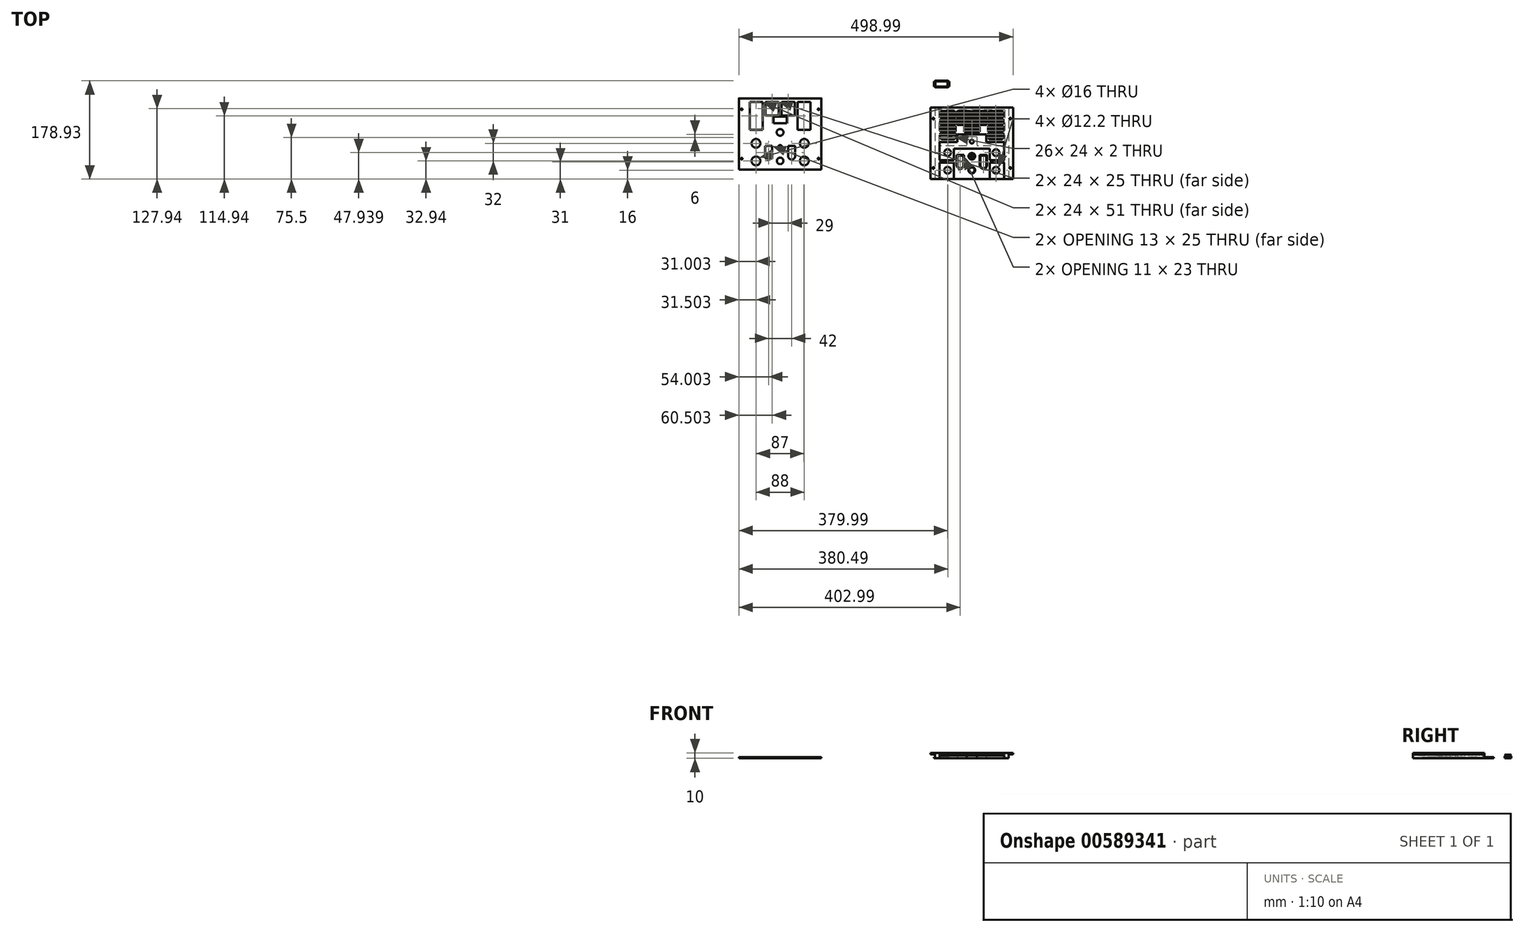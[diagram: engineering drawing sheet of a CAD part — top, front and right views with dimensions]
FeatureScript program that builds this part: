
annotation { "Feature Type Name" : "Feature", "Feature Type Description" : "" }
export const myFeature = defineFeature(function(context is Context, id is Id, definition is map)
    precondition{}
    {
        {
            var Q0;
            Q0=qCreatedBy(makeId("Top.planeOp"),FACE);
            var sketch = newSketch(context, id + "F0", { "sketchPlane" : qUnion([Q0])});
            skLineSegment(sketch, "E0.bottom", {"start": v(75, -65) * mm, "end": v(-75, -65) * mm});
            skLineSegment(sketch, "E0.top", {"start": v(75, 65) * mm, "end": v(-75, 65) * mm});
            skLineSegment(sketch, "E0.left", {"start": v(75, -65) * mm, "end": v(75, 65) * mm});
            skLineSegment(sketch, "E0.right", {"start": v(-75, -65) * mm, "end": v(-75, 65) * mm});
            skPoint(sketch, "E0.middle", {"position": v(0, 0) * mm});
            skLineSegment(sketch, "E1.bottom", {"start": v(-75, 65) * mm, "end": v(-65, 65) * mm, "construction": true});
            skLineSegment(sketch, "E1.top", {"start": v(-75, -65) * mm, "end": v(-65, -65) * mm, "construction": true});
            skLineSegment(sketch, "E1.left", {"start": v(-75, 65) * mm, "end": v(-75, -65) * mm, "construction": true});
            skLineSegment(sketch, "E1.right", {"start": v(-65, 65) * mm, "end": v(-65, -65) * mm, "construction": true});
            skLineSegment(sketch, "E2.bottom", {"start": v(75, -65) * mm, "end": v(65, -65) * mm, "construction": true});
            skLineSegment(sketch, "E2.top", {"start": v(75, 65) * mm, "end": v(65, 65) * mm, "construction": true});
            skLineSegment(sketch, "E2.left", {"start": v(75, -65) * mm, "end": v(75, 65) * mm, "construction": true});
            skLineSegment(sketch, "E2.right", {"start": v(65, -65) * mm, "end": v(65, 65) * mm, "construction": true});
            skCircle(sketch, "E3", {"center": v(-44, -17) * mm, "radius": 6.1 * mm});
            skCircle(sketch, "E4", {"center": v(-44, -49) * mm, "radius": 6.1 * mm});
            skCircle(sketch, "E5", {"center": v(44, -17) * mm, "radius": 6.1 * mm});
            skCircle(sketch, "E6", {"center": v(44, -49) * mm, "radius": 6.1 * mm});
            skCircle(sketch, "E7", {"center": v(0, -49) * mm, "radius": 6 * mm});
            skCircle(sketch, "E8", {"center": v(0, -23.67) * mm, "radius": 6 * mm});
            skLineSegment(sketch, "E9.bottom", {"start": v(-27.5, -21.5) * mm, "end": v(-14.5, -21.5) * mm});
            skLineSegment(sketch, "E9.top", {"start": v(-21, -46.5) * mm, "end": v(-21, -46.5) * mm});
            skLineSegment(sketch, "E9.left", {"start": v(-27.5, -21.5) * mm, "end": v(-27.5, -40) * mm});
            skLineSegment(sketch, "E9.right", {"start": v(-14.5, -21.5) * mm, "end": v(-14.5, -40) * mm});
            skPoint(sketch, "E10.visualSharp", {"position": v(-27.5, -46.5) * mm});
            skArc(sketch, "E10.filletArc", {"start": v(-27.5, -40) * mm, "mid": v(-25.6, -44.6) * mm, "end": v(-21, -46.5) * mm});
            skPoint(sketch, "E11.visualSharp", {"position": v(-14.5, -46.5) * mm});
            skArc(sketch, "E11.filletArc", {"start": v(-21, -46.5) * mm, "mid": v(-16.4, -44.6) * mm, "end": v(-14.5, -40) * mm});
            skLineSegment(sketch, "E12.bottom", {"start": v(14.5, -21.5) * mm, "end": v(27.5, -21.5) * mm});
            skLineSegment(sketch, "E12.top", {"start": v(21, -46.5) * mm, "end": v(21, -46.5) * mm});
            skLineSegment(sketch, "E12.left", {"start": v(14.5, -21.5) * mm, "end": v(14.5, -40) * mm});
            skLineSegment(sketch, "E12.right", {"start": v(27.5, -21.5) * mm, "end": v(27.5, -40) * mm});
            skPoint(sketch, "E13.visualSharp", {"position": v(14.5, -46.5) * mm});
            skArc(sketch, "E13.filletArc", {"start": v(14.5, -40) * mm, "mid": v(16.4, -44.6) * mm, "end": v(21, -46.5) * mm});
            skPoint(sketch, "E14.visualSharp", {"position": v(27.5, -46.5) * mm});
            skArc(sketch, "E14.filletArc", {"start": v(21, -46.5) * mm, "mid": v(25.6, -44.6) * mm, "end": v(27.5, -40) * mm});
            skLineSegment(sketch, "E15.bottom", {"start": v(56.5, 6.5) * mm, "end": v(-56.5, 6.5) * mm});
            skLineSegment(sketch, "E15.top", {"start": v(56.5, 59.5) * mm, "end": v(-56.5, 59.5) * mm, "construction": true});
            skLineSegment(sketch, "E15.left", {"start": v(56.5, 6.5) * mm, "end": v(56.5, 59.5) * mm, "construction": true});
            skLineSegment(sketch, "E15.right", {"start": v(-56.5, 6.5) * mm, "end": v(-56.5, 59.5) * mm, "construction": true});
            skPoint(sketch, "E15.middle", {"position": v(0, 33) * mm});
            skCircle(sketch, "E16", {"center": v(-44, -17) * mm, "radius": 8 * mm, "construction": true});
            skCircle(sketch, "E17", {"center": v(-44, -49) * mm, "radius": 8 * mm, "construction": true});
            skCircle(sketch, "E18", {"center": v(44, -49) * mm, "radius": 8 * mm, "construction": true});
            skCircle(sketch, "E19", {"center": v(44, -17) * mm, "radius": 8 * mm, "construction": true});
            skLineSegment(sketch, "E20.bottom", {"start": v(-31.5, 46.5) * mm, "end": v(-55.5, 46.5) * mm, "construction": true});
            skLineSegment(sketch, "E20.top", {"start": v(-31.5, 58.5) * mm, "end": v(-55.5, 58.5) * mm, "construction": true});
            skLineSegment(sketch, "E20.left", {"start": v(-31.5, 46.5) * mm, "end": v(-31.5, 58.5) * mm, "construction": true});
            skLineSegment(sketch, "E20.right", {"start": v(-55.5, 46.5) * mm, "end": v(-55.5, 58.5) * mm, "construction": true});
            skPoint(sketch, "E20.middle", {"position": v(-43.5, 52.5) * mm});
            skLineSegment(sketch, "E21.bottom", {"start": v(-31.5, 45.5) * mm, "end": v(-55.5, 45.5) * mm, "construction": true});
            skLineSegment(sketch, "E21.top", {"start": v(-31.5, 33.5) * mm, "end": v(-55.5, 33.5) * mm, "construction": true});
            skLineSegment(sketch, "E21.left", {"start": v(-31.5, 45.5) * mm, "end": v(-31.5, 33.5) * mm, "construction": true});
            skLineSegment(sketch, "E21.right", {"start": v(-55.5, 45.5) * mm, "end": v(-55.5, 33.5) * mm, "construction": true});
            skPoint(sketch, "E21.middle", {"position": v(-43.5, 39.5) * mm});
            skLineSegment(sketch, "E22.bottom", {"start": v(-31.5, 32.5) * mm, "end": v(-55.5, 32.5) * mm, "construction": true});
            skLineSegment(sketch, "E22.top", {"start": v(-31.5, 20.5) * mm, "end": v(-55.5, 20.5) * mm, "construction": true});
            skLineSegment(sketch, "E22.left", {"start": v(-31.5, 32.5) * mm, "end": v(-31.5, 20.5) * mm, "construction": true});
            skLineSegment(sketch, "E22.right", {"start": v(-55.5, 32.5) * mm, "end": v(-55.5, 20.5) * mm, "construction": true});
            skPoint(sketch, "E22.middle", {"position": v(-43.5, 26.5) * mm});
            skLineSegment(sketch, "E23.bottom", {"start": v(-31.5, 19.5) * mm, "end": v(-55.5, 19.5) * mm, "construction": true});
            skLineSegment(sketch, "E23.top", {"start": v(-31.5, 7.5) * mm, "end": v(-55.5, 7.5) * mm, "construction": true});
            skLineSegment(sketch, "E23.left", {"start": v(-31.5, 19.5) * mm, "end": v(-31.5, 7.5) * mm, "construction": true});
            skLineSegment(sketch, "E23.right", {"start": v(-55.5, 19.5) * mm, "end": v(-55.5, 7.5) * mm, "construction": true});
            skPoint(sketch, "E23.middle", {"position": v(-43.5, 13.5) * mm});
            skLineSegment(sketch, "E24.bottom", {"start": v(55.5, 32.5) * mm, "end": v(31.5, 32.5) * mm, "construction": true});
            skLineSegment(sketch, "E24.top", {"start": v(55.5, 20.5) * mm, "end": v(31.5, 20.5) * mm, "construction": true});
            skLineSegment(sketch, "E24.left", {"start": v(55.5, 32.5) * mm, "end": v(55.5, 20.5) * mm, "construction": true});
            skLineSegment(sketch, "E24.right", {"start": v(31.5, 32.5) * mm, "end": v(31.5, 20.5) * mm, "construction": true});
            skPoint(sketch, "E24.middle", {"position": v(43.5, 26.5) * mm});
            skLineSegment(sketch, "E25.bottom", {"start": v(55.5, 19.5) * mm, "end": v(31.5, 19.5) * mm, "construction": true});
            skLineSegment(sketch, "E25.top", {"start": v(55.5, 7.5) * mm, "end": v(31.5, 7.5) * mm, "construction": true});
            skLineSegment(sketch, "E25.left", {"start": v(55.5, 19.5) * mm, "end": v(55.5, 7.5) * mm, "construction": true});
            skLineSegment(sketch, "E25.right", {"start": v(31.5, 19.5) * mm, "end": v(31.5, 7.5) * mm, "construction": true});
            skPoint(sketch, "E25.middle", {"position": v(43.5, 13.5) * mm});
            skPoint(sketch, "E25.middle.positionSnap0", {"position": v(43.5, 20.5) * mm});
            skPoint(sketch, "E25.centerSnap0", {"position": v(43.5, 20.5) * mm});
            skLineSegment(sketch, "E26.bottom", {"start": v(12, 20.33) * mm, "end": v(-12, 20.33) * mm, "construction": true});
            skLineSegment(sketch, "E26.top", {"start": v(12, 32.33) * mm, "end": v(-12, 32.33) * mm, "construction": true});
            skLineSegment(sketch, "E26.left", {"start": v(12, 20.33) * mm, "end": v(12, 32.33) * mm, "construction": true});
            skLineSegment(sketch, "E26.right", {"start": v(-12, 20.33) * mm, "end": v(-12, 32.33) * mm, "construction": true});
            skPoint(sketch, "E26.middle", {"position": v(0, 26.33) * mm});
            skCircle(sketch, "E27", {"center": v(-70, 45) * mm, "radius": 1.5 * mm});
            skCircle(sketch, "E28", {"center": v(-70, -45) * mm, "radius": 1.5 * mm});
            skCircle(sketch, "E29", {"center": v(70, 45) * mm, "radius": 1.5 * mm});
            skCircle(sketch, "E30", {"center": v(70, -45) * mm, "radius": 1.5 * mm});
            skCircle(sketch, "E31", {"center": v(0, 3) * mm, "radius": 3.5 * mm});
            skCircle(sketch, "E32", {"center": v(0, 3) * mm, "radius": 6.15 * mm, "construction": true});
            skLineSegment(sketch, "E33.bottom", {"start": v(-30.46, 6.5) * mm, "end": v(-12.96, 6.5) * mm});
            skLineSegment(sketch, "E33.top", {"start": v(-30.46, 32.33) * mm, "end": v(-12.96, 32.33) * mm, "construction": true});
            skLineSegment(sketch, "E33.left", {"start": v(-30.46, 6.5) * mm, "end": v(-30.46, 32.33) * mm, "construction": true});
            skLineSegment(sketch, "E33.right", {"start": v(-12.96, 19.33) * mm, "end": v(-12.96, 32.33) * mm, "construction": true});
            skLineSegment(sketch, "E34.bottom", {"start": v(13.04, 32.33) * mm, "end": v(30.54, 32.33) * mm, "construction": true});
            skLineSegment(sketch, "E34.top", {"start": v(13.04, 6.5) * mm, "end": v(30.54, 6.5) * mm});
            skLineSegment(sketch, "E34.left", {"start": v(13.04, 32.33) * mm, "end": v(13.04, 19.33) * mm, "construction": true});
            skLineSegment(sketch, "E34.right", {"start": v(30.54, 32.33) * mm, "end": v(30.54, 6.5) * mm, "construction": true});
            skLineSegment(sketch, "E35", {"start": v(-12.96, 19.33) * mm, "end": v(13.04, 19.33) * mm, "construction": true});
            skLineSegment(sketch, "E36.bottom", {"start": v(-55.5, 57.5) * mm, "end": v(-57.5, 57.5) * mm, "construction": true});
            skLineSegment(sketch, "E36.top", {"start": v(-55.5, 47.5) * mm, "end": v(-57.5, 47.5) * mm, "construction": true});
            skLineSegment(sketch, "E36.left", {"start": v(-55.5, 57.5) * mm, "end": v(-55.5, 47.5) * mm, "construction": true});
            skLineSegment(sketch, "E36.right", {"start": v(-57.5, 57.5) * mm, "end": v(-57.5, 47.5) * mm, "construction": true});
            skLineSegment(sketch, "E37.bottom", {"start": v(-31.5, 57.5) * mm, "end": v(-29.5, 57.5) * mm, "construction": true});
            skLineSegment(sketch, "E37.top", {"start": v(-31.5, 47.5) * mm, "end": v(-29.5, 47.5) * mm, "construction": true});
            skLineSegment(sketch, "E37.left", {"start": v(-31.5, 57.5) * mm, "end": v(-31.5, 47.5) * mm, "construction": true});
            skLineSegment(sketch, "E37.right", {"start": v(-29.5, 57.5) * mm, "end": v(-29.5, 47.5) * mm, "construction": true});
            skLineSegment(sketch, "E38.bottom", {"start": v(-55.5, 44.5) * mm, "end": v(-57.5, 44.5) * mm, "construction": true});
            skLineSegment(sketch, "E38.top", {"start": v(-55.5, 34.5) * mm, "end": v(-57.5, 34.5) * mm, "construction": true});
            skLineSegment(sketch, "E38.left", {"start": v(-55.5, 44.5) * mm, "end": v(-55.5, 34.5) * mm, "construction": true});
            skLineSegment(sketch, "E38.right", {"start": v(-57.5, 44.5) * mm, "end": v(-57.5, 34.5) * mm, "construction": true});
            skLineSegment(sketch, "E39.bottom", {"start": v(-31.5, 44.5) * mm, "end": v(-29.5, 44.5) * mm, "construction": true});
            skLineSegment(sketch, "E39.top", {"start": v(-31.5, 34.5) * mm, "end": v(-29.5, 34.5) * mm, "construction": true});
            skLineSegment(sketch, "E39.left", {"start": v(-31.5, 44.5) * mm, "end": v(-31.5, 34.5) * mm, "construction": true});
            skLineSegment(sketch, "E39.right", {"start": v(-29.5, 44.5) * mm, "end": v(-29.5, 34.5) * mm, "construction": true});
            skPoint(sketch, "E40.1.0.0", {"position": v(-14.5, 39.5) * mm});
            skLineSegment(sketch, "E40.1.0.1", {"start": v(-2.5, 44.5) * mm, "end": v(-2.5, 34.5) * mm, "construction": true});
            skLineSegment(sketch, "E40.1.0.2", {"start": v(-2.5, 45.5) * mm, "end": v(-26.5, 45.5) * mm, "construction": true});
            skLineSegment(sketch, "E40.1.0.3", {"start": v(-26.5, 44.5) * mm, "end": v(-26.5, 34.5) * mm, "construction": true});
            skLineSegment(sketch, "E40.1.0.4", {"start": v(-2.5, 58.5) * mm, "end": v(-26.5, 58.5) * mm, "construction": true});
            skLineSegment(sketch, "E40.1.0.5", {"start": v(-0.5, 44.5) * mm, "end": v(-0.5, 34.5) * mm, "construction": true});
            skLineSegment(sketch, "E40.1.0.6", {"start": v(-2.5, 47.5) * mm, "end": v(-0.5, 47.5) * mm, "construction": true});
            skLineSegment(sketch, "E40.1.0.7", {"start": v(-26.5, 57.5) * mm, "end": v(-26.5, 47.5) * mm, "construction": true});
            skLineSegment(sketch, "E40.1.0.8", {"start": v(-2.5, 46.5) * mm, "end": v(-26.5, 46.5) * mm, "construction": true});
            skLineSegment(sketch, "E40.1.0.9", {"start": v(-2.5, 33.5) * mm, "end": v(-26.5, 33.5) * mm, "construction": true});
            skLineSegment(sketch, "E40.1.0.10", {"start": v(-28.5, 44.5) * mm, "end": v(-28.5, 34.5) * mm, "construction": true});
            skLineSegment(sketch, "E40.1.0.11", {"start": v(-26.5, 47.5) * mm, "end": v(-28.5, 47.5) * mm, "construction": true});
            skLineSegment(sketch, "E40.1.0.12", {"start": v(-28.5, 57.5) * mm, "end": v(-28.5, 47.5) * mm, "construction": true});
            skLineSegment(sketch, "E40.1.0.13", {"start": v(-26.5, 34.5) * mm, "end": v(-28.5, 34.5) * mm, "construction": true});
            skLineSegment(sketch, "E40.1.0.14", {"start": v(-0.5, 57.5) * mm, "end": v(-0.5, 47.5) * mm, "construction": true});
            skLineSegment(sketch, "E40.1.0.15", {"start": v(-2.5, 46.5) * mm, "end": v(-2.5, 58.5) * mm, "construction": true});
            skLineSegment(sketch, "E40.1.0.16", {"start": v(-2.5, 44.5) * mm, "end": v(-0.5, 44.5) * mm, "construction": true});
            skLineSegment(sketch, "E40.1.0.17", {"start": v(-2.5, 57.5) * mm, "end": v(-0.5, 57.5) * mm, "construction": true});
            skLineSegment(sketch, "E40.1.0.18", {"start": v(-2.5, 34.5) * mm, "end": v(-0.5, 34.5) * mm, "construction": true});
            skLineSegment(sketch, "E40.1.0.19", {"start": v(-26.5, 57.5) * mm, "end": v(-28.5, 57.5) * mm, "construction": true});
            skPoint(sketch, "E40.1.0.20", {"position": v(-14.5, 52.5) * mm});
            skLineSegment(sketch, "E40.1.0.21", {"start": v(-26.5, 44.5) * mm, "end": v(-28.5, 44.5) * mm, "construction": true});
            skLineSegment(sketch, "E40.1.0.22", {"start": v(-2.5, 57.5) * mm, "end": v(-2.5, 47.5) * mm, "construction": true});
            skLineSegment(sketch, "E40.1.0.23", {"start": v(-26.5, 46.5) * mm, "end": v(-26.5, 58.5) * mm, "construction": true});
            skLineSegment(sketch, "E40.1.0.24", {"start": v(-26.5, 45.5) * mm, "end": v(-26.5, 33.5) * mm, "construction": true});
            skLineSegment(sketch, "E40.1.0.25", {"start": v(-2.5, 45.5) * mm, "end": v(-2.5, 33.5) * mm, "construction": true});
            skPoint(sketch, "E40.2.0.0", {"position": v(14.5, 39.5) * mm});
            skLineSegment(sketch, "E40.2.0.1", {"start": v(26.5, 44.5) * mm, "end": v(26.5, 34.5) * mm, "construction": true});
            skLineSegment(sketch, "E40.2.0.2", {"start": v(26.5, 45.5) * mm, "end": v(2.5, 45.5) * mm, "construction": true});
            skLineSegment(sketch, "E40.2.0.3", {"start": v(2.5, 44.5) * mm, "end": v(2.5, 34.5) * mm, "construction": true});
            skLineSegment(sketch, "E40.2.0.4", {"start": v(26.5, 58.5) * mm, "end": v(2.5, 58.5) * mm, "construction": true});
            skLineSegment(sketch, "E40.2.0.5", {"start": v(28.5, 44.5) * mm, "end": v(28.5, 34.5) * mm, "construction": true});
            skLineSegment(sketch, "E40.2.0.6", {"start": v(26.5, 47.5) * mm, "end": v(28.5, 47.5) * mm, "construction": true});
            skLineSegment(sketch, "E40.2.0.7", {"start": v(2.5, 57.5) * mm, "end": v(2.5, 47.5) * mm, "construction": true});
            skLineSegment(sketch, "E40.2.0.8", {"start": v(26.5, 46.5) * mm, "end": v(2.5, 46.5) * mm, "construction": true});
            skLineSegment(sketch, "E40.2.0.9", {"start": v(26.5, 33.5) * mm, "end": v(2.5, 33.5) * mm, "construction": true});
            skLineSegment(sketch, "E40.2.0.10", {"start": v(0.5, 44.5) * mm, "end": v(0.5, 34.5) * mm, "construction": true});
            skLineSegment(sketch, "E40.2.0.11", {"start": v(2.5, 47.5) * mm, "end": v(0.5, 47.5) * mm, "construction": true});
            skLineSegment(sketch, "E40.2.0.12", {"start": v(0.5, 57.5) * mm, "end": v(0.5, 47.5) * mm, "construction": true});
            skLineSegment(sketch, "E40.2.0.13", {"start": v(2.5, 34.5) * mm, "end": v(0.5, 34.5) * mm, "construction": true});
            skLineSegment(sketch, "E40.2.0.14", {"start": v(28.5, 57.5) * mm, "end": v(28.5, 47.5) * mm, "construction": true});
            skLineSegment(sketch, "E40.2.0.15", {"start": v(26.5, 46.5) * mm, "end": v(26.5, 58.5) * mm, "construction": true});
            skLineSegment(sketch, "E40.2.0.16", {"start": v(26.5, 44.5) * mm, "end": v(28.5, 44.5) * mm, "construction": true});
            skLineSegment(sketch, "E40.2.0.17", {"start": v(26.5, 57.5) * mm, "end": v(28.5, 57.5) * mm, "construction": true});
            skLineSegment(sketch, "E40.2.0.18", {"start": v(26.5, 34.5) * mm, "end": v(28.5, 34.5) * mm, "construction": true});
            skLineSegment(sketch, "E40.2.0.19", {"start": v(2.5, 57.5) * mm, "end": v(0.5, 57.5) * mm, "construction": true});
            skPoint(sketch, "E40.2.0.20", {"position": v(14.5, 52.5) * mm});
            skLineSegment(sketch, "E40.2.0.21", {"start": v(2.5, 44.5) * mm, "end": v(0.5, 44.5) * mm, "construction": true});
            skLineSegment(sketch, "E40.2.0.22", {"start": v(26.5, 57.5) * mm, "end": v(26.5, 47.5) * mm, "construction": true});
            skLineSegment(sketch, "E40.2.0.23", {"start": v(2.5, 46.5) * mm, "end": v(2.5, 58.5) * mm, "construction": true});
            skLineSegment(sketch, "E40.2.0.24", {"start": v(2.5, 45.5) * mm, "end": v(2.5, 33.5) * mm, "construction": true});
            skLineSegment(sketch, "E40.2.0.25", {"start": v(26.5, 45.5) * mm, "end": v(26.5, 33.5) * mm, "construction": true});
            skPoint(sketch, "E40.3.0.0", {"position": v(43.5, 39.5) * mm});
            skLineSegment(sketch, "E40.3.0.1", {"start": v(55.5, 44.5) * mm, "end": v(55.5, 34.5) * mm, "construction": true});
            skLineSegment(sketch, "E40.3.0.2", {"start": v(55.5, 45.5) * mm, "end": v(31.5, 45.5) * mm, "construction": true});
            skLineSegment(sketch, "E40.3.0.3", {"start": v(31.5, 44.5) * mm, "end": v(31.5, 34.5) * mm, "construction": true});
            skLineSegment(sketch, "E40.3.0.4", {"start": v(55.5, 58.5) * mm, "end": v(31.5, 58.5) * mm, "construction": true});
            skLineSegment(sketch, "E40.3.0.5", {"start": v(57.5, 44.5) * mm, "end": v(57.5, 34.5) * mm, "construction": true});
            skLineSegment(sketch, "E40.3.0.6", {"start": v(55.5, 47.5) * mm, "end": v(57.5, 47.5) * mm, "construction": true});
            skLineSegment(sketch, "E40.3.0.7", {"start": v(31.5, 57.5) * mm, "end": v(31.5, 47.5) * mm, "construction": true});
            skLineSegment(sketch, "E40.3.0.8", {"start": v(55.5, 46.5) * mm, "end": v(31.5, 46.5) * mm, "construction": true});
            skLineSegment(sketch, "E40.3.0.9", {"start": v(55.5, 33.5) * mm, "end": v(31.5, 33.5) * mm, "construction": true});
            skLineSegment(sketch, "E40.3.0.10", {"start": v(29.5, 44.5) * mm, "end": v(29.5, 34.5) * mm, "construction": true});
            skLineSegment(sketch, "E40.3.0.11", {"start": v(31.5, 47.5) * mm, "end": v(29.5, 47.5) * mm, "construction": true});
            skLineSegment(sketch, "E40.3.0.12", {"start": v(29.5, 57.5) * mm, "end": v(29.5, 47.5) * mm, "construction": true});
            skLineSegment(sketch, "E40.3.0.13", {"start": v(31.5, 34.5) * mm, "end": v(29.5, 34.5) * mm, "construction": true});
            skLineSegment(sketch, "E40.3.0.14", {"start": v(57.5, 57.5) * mm, "end": v(57.5, 47.5) * mm, "construction": true});
            skLineSegment(sketch, "E40.3.0.15", {"start": v(55.5, 46.5) * mm, "end": v(55.5, 58.5) * mm, "construction": true});
            skLineSegment(sketch, "E40.3.0.16", {"start": v(55.5, 44.5) * mm, "end": v(57.5, 44.5) * mm, "construction": true});
            skLineSegment(sketch, "E40.3.0.17", {"start": v(55.5, 57.5) * mm, "end": v(57.5, 57.5) * mm, "construction": true});
            skLineSegment(sketch, "E40.3.0.18", {"start": v(55.5, 34.5) * mm, "end": v(57.5, 34.5) * mm, "construction": true});
            skLineSegment(sketch, "E40.3.0.19", {"start": v(31.5, 57.5) * mm, "end": v(29.5, 57.5) * mm, "construction": true});
            skPoint(sketch, "E40.3.0.20", {"position": v(43.5, 52.5) * mm});
            skLineSegment(sketch, "E40.3.0.21", {"start": v(31.5, 44.5) * mm, "end": v(29.5, 44.5) * mm, "construction": true});
            skLineSegment(sketch, "E40.3.0.22", {"start": v(55.5, 57.5) * mm, "end": v(55.5, 47.5) * mm, "construction": true});
            skLineSegment(sketch, "E40.3.0.23", {"start": v(31.5, 46.5) * mm, "end": v(31.5, 58.5) * mm, "construction": true});
            skLineSegment(sketch, "E40.3.0.24", {"start": v(31.5, 45.5) * mm, "end": v(31.5, 33.5) * mm, "construction": true});
            skLineSegment(sketch, "E40.3.0.25", {"start": v(55.5, 45.5) * mm, "end": v(55.5, 33.5) * mm, "construction": true});
            skLineSegment(sketch, "E40.direction1", {"start": v(-57.5, 34.5) * mm, "end": v(-28.5, 34.5) * mm, "construction": true});
            skSolve(sketch);
        }
        {
            var Q0;
            Q0=makeQuery(id+"F0.imprint","IMPRINT",FACE,{"disambiguationData":[TD([[makeQuery(id+"F0.imprint","IMPRINT",EDGE,{"derivedFrom":sQuery(id+"F0.wireOp",EDGE,"E0.bottom")}),-1.0]])]});
            var Q1;
            {var subQ3=sQuery(id+"F0.wireOp",EDGE,"E33.bottom");Q1=makeQuery(id+"F0.imprint","IMPRINT",FACE,{"disambiguationData":[TD([[makeQuery(id+"F0.imprint","IMPRINT",EDGE,{"derivedFrom":subQ3}),1.0]])]});}
            extrude(context, id + "F1", {"entities" : qUnion([Q0, Q1]), "depth" : 10 * mm});
        }
        {
            var Q0;
            Q0=qCreatedBy(makeId("Top.planeOp"),FACE);
            var sketch = newSketch(context, id + "F2", { "sketchPlane" : qUnion([Q0])});
            skLineSegment(sketch, "E41.bottom", {"start": v(-273.99, -48.06) * mm, "end": v(-423.99, -48.06) * mm});
            skLineSegment(sketch, "E41.top", {"start": v(-273.99, 81.94) * mm, "end": v(-423.99, 81.94) * mm});
            skLineSegment(sketch, "E41.left", {"start": v(-273.99, -48.06) * mm, "end": v(-273.99, 81.94) * mm});
            skLineSegment(sketch, "E41.right", {"start": v(-423.99, -48.06) * mm, "end": v(-423.99, 81.94) * mm});
            skPoint(sketch, "E41.middle", {"position": v(-348.99, 16.94) * mm});
            skLineSegment(sketch, "E42.bottom", {"start": v(-423.99, 81.94) * mm, "end": v(-413.99, 81.94) * mm, "construction": true});
            skLineSegment(sketch, "E42.top", {"start": v(-423.99, -48.06) * mm, "end": v(-413.99, -48.06) * mm, "construction": true});
            skLineSegment(sketch, "E42.left", {"start": v(-423.99, 81.94) * mm, "end": v(-423.99, -48.06) * mm, "construction": true});
            skLineSegment(sketch, "E42.right", {"start": v(-413.99, 81.94) * mm, "end": v(-413.99, -48.06) * mm, "construction": true});
            skLineSegment(sketch, "E43.bottom", {"start": v(-273.99, -48.06) * mm, "end": v(-283.99, -48.06) * mm, "construction": true});
            skLineSegment(sketch, "E43.top", {"start": v(-273.99, 81.94) * mm, "end": v(-283.99, 81.94) * mm, "construction": true});
            skLineSegment(sketch, "E43.left", {"start": v(-273.99, -48.06) * mm, "end": v(-273.99, 81.94) * mm, "construction": true});
            skLineSegment(sketch, "E43.right", {"start": v(-283.99, -48.06) * mm, "end": v(-283.99, 81.94) * mm, "construction": true});
            skCircle(sketch, "E44", {"center": v(-392.99, -0.06) * mm, "radius": 6.1 * mm, "construction": true});
            skCircle(sketch, "E45", {"center": v(-392.99, -32.06) * mm, "radius": 6.1 * mm, "construction": true});
            skCircle(sketch, "E46", {"center": v(-304.99, -0.06) * mm, "radius": 6.1 * mm, "construction": true});
            skCircle(sketch, "E47", {"center": v(-304.99, -32.06) * mm, "radius": 6.1 * mm, "construction": true});
            skCircle(sketch, "E48", {"center": v(-348.99, -32.06) * mm, "radius": 6 * mm});
            skCircle(sketch, "E49", {"center": v(-348.99, -6.73) * mm, "radius": 3.5 * mm});
            skLineSegment(sketch, "E50.bottom", {"start": v(-376.49, -4.56) * mm, "end": v(-363.49, -4.56) * mm});
            skLineSegment(sketch, "E50.top", {"start": v(-369.99, -29.56) * mm, "end": v(-369.99, -29.56) * mm});
            skLineSegment(sketch, "E50.left", {"start": v(-376.49, -4.56) * mm, "end": v(-376.49, -23.06) * mm});
            skLineSegment(sketch, "E50.right", {"start": v(-363.49, -4.56) * mm, "end": v(-363.49, -23.06) * mm});
            skPoint(sketch, "E51.visualSharp", {"position": v(-376.49, -29.56) * mm});
            skArc(sketch, "E51.filletArc", {"start": v(-376.49, -23.06) * mm, "mid": v(-374.58, -27.66) * mm, "end": v(-369.99, -29.56) * mm});
            skPoint(sketch, "E52.visualSharp", {"position": v(-363.49, -29.56) * mm});
            skArc(sketch, "E52.filletArc", {"start": v(-369.99, -29.56) * mm, "mid": v(-365.4, -27.66) * mm, "end": v(-363.49, -23.06) * mm});
            skLineSegment(sketch, "E53.bottom", {"start": v(-334.49, -4.56) * mm, "end": v(-321.49, -4.56) * mm});
            skLineSegment(sketch, "E53.top", {"start": v(-327.99, -29.56) * mm, "end": v(-327.99, -29.56) * mm});
            skLineSegment(sketch, "E53.left", {"start": v(-334.49, -4.56) * mm, "end": v(-334.49, -23.06) * mm});
            skLineSegment(sketch, "E53.right", {"start": v(-321.49, -4.56) * mm, "end": v(-321.49, -23.06) * mm});
            skPoint(sketch, "E54.visualSharp", {"position": v(-334.49, -29.56) * mm});
            skArc(sketch, "E54.filletArc", {"start": v(-334.49, -23.06) * mm, "mid": v(-332.58, -27.66) * mm, "end": v(-327.99, -29.56) * mm});
            skPoint(sketch, "E55.visualSharp", {"position": v(-321.49, -29.56) * mm});
            skArc(sketch, "E55.filletArc", {"start": v(-327.99, -29.56) * mm, "mid": v(-323.4, -27.66) * mm, "end": v(-321.49, -23.06) * mm});
            skPoint(sketch, "E56.middle", {"position": v(-348.99, 49.94) * mm});
            skCircle(sketch, "E57", {"center": v(-392.99, -0.06) * mm, "radius": 8 * mm});
            skCircle(sketch, "E58", {"center": v(-392.99, -32.06) * mm, "radius": 8 * mm});
            skCircle(sketch, "E59", {"center": v(-304.99, -32.06) * mm, "radius": 8 * mm});
            skCircle(sketch, "E60", {"center": v(-304.99, -0.06) * mm, "radius": 8 * mm});
            skLineSegment(sketch, "E61.bottom", {"start": v(-380.49, 63.44) * mm, "end": v(-404.49, 63.44) * mm, "construction": true});
            skLineSegment(sketch, "E61.top", {"start": v(-380.49, 75.44) * mm, "end": v(-404.49, 75.44) * mm, "construction": true});
            skLineSegment(sketch, "E61.left", {"start": v(-380.49, 63.44) * mm, "end": v(-380.49, 75.44) * mm, "construction": true});
            skLineSegment(sketch, "E61.right", {"start": v(-404.49, 63.44) * mm, "end": v(-404.49, 75.44) * mm, "construction": true});
            skPoint(sketch, "E61.middle", {"position": v(-392.49, 69.44) * mm});
            skLineSegment(sketch, "E62.bottom", {"start": v(-380.49, 62.44) * mm, "end": v(-404.49, 62.44) * mm, "construction": true});
            skLineSegment(sketch, "E62.top", {"start": v(-380.49, 50.44) * mm, "end": v(-404.49, 50.44) * mm, "construction": true});
            skLineSegment(sketch, "E62.left", {"start": v(-380.49, 62.44) * mm, "end": v(-380.49, 50.44) * mm, "construction": true});
            skLineSegment(sketch, "E62.right", {"start": v(-404.49, 62.44) * mm, "end": v(-404.49, 50.44) * mm, "construction": true});
            skPoint(sketch, "E62.middle", {"position": v(-392.49, 56.44) * mm});
            skLineSegment(sketch, "E63.bottom", {"start": v(-380.49, 49.44) * mm, "end": v(-404.49, 49.44) * mm, "construction": true});
            skLineSegment(sketch, "E63.top", {"start": v(-380.49, 37.44) * mm, "end": v(-404.49, 37.44) * mm, "construction": true});
            skLineSegment(sketch, "E63.left", {"start": v(-380.49, 49.44) * mm, "end": v(-380.49, 37.44) * mm, "construction": true});
            skLineSegment(sketch, "E63.right", {"start": v(-404.49, 49.44) * mm, "end": v(-404.49, 37.44) * mm, "construction": true});
            skPoint(sketch, "E63.middle", {"position": v(-392.49, 43.44) * mm});
            skLineSegment(sketch, "E64.bottom", {"start": v(-380.49, 36.44) * mm, "end": v(-404.49, 36.44) * mm, "construction": true});
            skLineSegment(sketch, "E64.top", {"start": v(-380.49, 24.44) * mm, "end": v(-404.49, 24.44) * mm, "construction": true});
            skLineSegment(sketch, "E64.left", {"start": v(-380.49, 36.44) * mm, "end": v(-380.49, 24.44) * mm, "construction": true});
            skLineSegment(sketch, "E64.right", {"start": v(-404.49, 36.44) * mm, "end": v(-404.49, 24.44) * mm, "construction": true});
            skPoint(sketch, "E64.middle", {"position": v(-392.49, 30.44) * mm});
            skPoint(sketch, "E65.1.0.0", {"position": v(-363.49, 56.44) * mm});
            skLineSegment(sketch, "E65.1.0.1", {"start": v(-351.49, 62.44) * mm, "end": v(-351.49, 50.44) * mm, "construction": true});
            skLineSegment(sketch, "E65.1.0.2", {"start": v(-351.49, 62.44) * mm, "end": v(-375.49, 62.44) * mm, "construction": true});
            skLineSegment(sketch, "E65.1.0.3", {"start": v(-375.49, 63.44) * mm, "end": v(-375.49, 75.44) * mm, "construction": true});
            skLineSegment(sketch, "E65.1.0.4", {"start": v(-351.49, 75.44) * mm, "end": v(-375.49, 75.44) * mm, "construction": true});
            skPoint(sketch, "E65.1.0.5", {"position": v(-363.49, 69.44) * mm});
            skLineSegment(sketch, "E65.1.0.6", {"start": v(-351.49, 50.44) * mm, "end": v(-375.49, 50.44) * mm, "construction": true});
            skLineSegment(sketch, "E65.1.0.7", {"start": v(-351.49, 63.44) * mm, "end": v(-351.49, 75.44) * mm, "construction": true});
            skLineSegment(sketch, "E65.1.0.8", {"start": v(-375.49, 62.44) * mm, "end": v(-375.49, 50.44) * mm, "construction": true});
            skLineSegment(sketch, "E65.1.0.9", {"start": v(-351.49, 63.44) * mm, "end": v(-375.49, 63.44) * mm, "construction": true});
            skPoint(sketch, "E65.2.0.0", {"position": v(-334.49, 56.44) * mm});
            skLineSegment(sketch, "E65.2.0.1", {"start": v(-322.49, 62.44) * mm, "end": v(-322.49, 50.44) * mm, "construction": true});
            skLineSegment(sketch, "E65.2.0.2", {"start": v(-322.49, 62.44) * mm, "end": v(-346.49, 62.44) * mm, "construction": true});
            skLineSegment(sketch, "E65.2.0.3", {"start": v(-346.49, 63.44) * mm, "end": v(-346.49, 75.44) * mm, "construction": true});
            skLineSegment(sketch, "E65.2.0.4", {"start": v(-322.49, 75.44) * mm, "end": v(-346.49, 75.44) * mm, "construction": true});
            skPoint(sketch, "E65.2.0.5", {"position": v(-334.49, 69.44) * mm});
            skLineSegment(sketch, "E65.2.0.6", {"start": v(-322.49, 50.44) * mm, "end": v(-346.49, 50.44) * mm, "construction": true});
            skLineSegment(sketch, "E65.2.0.7", {"start": v(-322.49, 63.44) * mm, "end": v(-322.49, 75.44) * mm, "construction": true});
            skLineSegment(sketch, "E65.2.0.8", {"start": v(-346.49, 62.44) * mm, "end": v(-346.49, 50.44) * mm, "construction": true});
            skLineSegment(sketch, "E65.2.0.9", {"start": v(-322.49, 63.44) * mm, "end": v(-346.49, 63.44) * mm, "construction": true});
            skPoint(sketch, "E65.3.0.0", {"position": v(-305.49, 56.44) * mm});
            skLineSegment(sketch, "E65.3.0.1", {"start": v(-293.49, 62.44) * mm, "end": v(-293.49, 50.44) * mm, "construction": true});
            skLineSegment(sketch, "E65.3.0.2", {"start": v(-293.49, 62.44) * mm, "end": v(-317.49, 62.44) * mm, "construction": true});
            skLineSegment(sketch, "E65.3.0.3", {"start": v(-317.49, 63.44) * mm, "end": v(-317.49, 75.44) * mm, "construction": true});
            skLineSegment(sketch, "E65.3.0.4", {"start": v(-293.49, 75.44) * mm, "end": v(-317.49, 75.44) * mm, "construction": true});
            skPoint(sketch, "E65.3.0.5", {"position": v(-305.49, 69.44) * mm});
            skLineSegment(sketch, "E65.3.0.6", {"start": v(-293.49, 50.44) * mm, "end": v(-317.49, 50.44) * mm, "construction": true});
            skLineSegment(sketch, "E65.3.0.7", {"start": v(-293.49, 63.44) * mm, "end": v(-293.49, 75.44) * mm, "construction": true});
            skLineSegment(sketch, "E65.3.0.8", {"start": v(-317.49, 62.44) * mm, "end": v(-317.49, 50.44) * mm, "construction": true});
            skLineSegment(sketch, "E65.3.0.9", {"start": v(-293.49, 63.44) * mm, "end": v(-317.49, 63.44) * mm, "construction": true});
            skLineSegment(sketch, "E65.direction1", {"start": v(-404.49, 50.44) * mm, "end": v(-375.49, 50.44) * mm, "construction": true});
            skLineSegment(sketch, "E66.bottom", {"start": v(-293.49, 49.44) * mm, "end": v(-317.49, 49.44) * mm, "construction": true});
            skLineSegment(sketch, "E66.top", {"start": v(-293.49, 37.44) * mm, "end": v(-317.49, 37.44) * mm, "construction": true});
            skLineSegment(sketch, "E66.left", {"start": v(-293.49, 49.44) * mm, "end": v(-293.49, 37.44) * mm, "construction": true});
            skLineSegment(sketch, "E66.right", {"start": v(-317.49, 49.44) * mm, "end": v(-317.49, 37.44) * mm, "construction": true});
            skPoint(sketch, "E66.middle", {"position": v(-305.49, 43.44) * mm});
            skLineSegment(sketch, "E67.bottom", {"start": v(-293.49, 36.44) * mm, "end": v(-317.49, 36.44) * mm, "construction": true});
            skLineSegment(sketch, "E67.top", {"start": v(-293.49, 24.44) * mm, "end": v(-317.49, 24.44) * mm, "construction": true});
            skLineSegment(sketch, "E67.left", {"start": v(-293.49, 36.44) * mm, "end": v(-293.49, 24.44) * mm, "construction": true});
            skLineSegment(sketch, "E67.right", {"start": v(-317.49, 36.44) * mm, "end": v(-317.49, 24.44) * mm, "construction": true});
            skPoint(sketch, "E67.middle", {"position": v(-305.49, 30.44) * mm});
            skPoint(sketch, "E67.middle.positionSnap0", {"position": v(-305.49, 37.44) * mm});
            skPoint(sketch, "E67.centerSnap0", {"position": v(-305.49, 37.44) * mm});
            skLineSegment(sketch, "E68.bottom", {"start": v(-336.99, 36.44) * mm, "end": v(-360.99, 36.44) * mm, "construction": true});
            skLineSegment(sketch, "E68.top", {"start": v(-336.99, 48.44) * mm, "end": v(-360.99, 48.44) * mm, "construction": true});
            skLineSegment(sketch, "E68.left", {"start": v(-336.99, 36.44) * mm, "end": v(-336.99, 48.44) * mm, "construction": true});
            skLineSegment(sketch, "E68.right", {"start": v(-360.99, 36.44) * mm, "end": v(-360.99, 48.44) * mm, "construction": true});
            skPoint(sketch, "E68.middle", {"position": v(-348.99, 42.44) * mm});
            skCircle(sketch, "E69", {"center": v(-418.99, 61.94) * mm, "radius": 1.5 * mm});
            skCircle(sketch, "E70", {"center": v(-418.99, -28.06) * mm, "radius": 1.5 * mm});
            skCircle(sketch, "E71", {"center": v(-278.99, 61.94) * mm, "radius": 1.5 * mm});
            skCircle(sketch, "E72", {"center": v(-278.99, -28.06) * mm, "radius": 1.5 * mm});
            skCircle(sketch, "E73", {"center": v(-348.99, 19.94) * mm, "radius": 3.5 * mm, "construction": true});
            skCircle(sketch, "E74", {"center": v(-348.99, 19.94) * mm, "radius": 6.15 * mm});
            skLineSegment(sketch, "E75", {"start": v(-404.49, 75.44) * mm, "end": v(-404.49, 24.44) * mm});
            skLineSegment(sketch, "E76", {"start": v(-404.49, 24.44) * mm, "end": v(-380.49, 24.44) * mm});
            skLineSegment(sketch, "E77", {"start": v(-380.49, 24.44) * mm, "end": v(-380.49, 50.44) * mm});
            skLineSegment(sketch, "E78", {"start": v(-380.49, 50.44) * mm, "end": v(-360.99, 50.44) * mm});
            skLineSegment(sketch, "E79", {"start": v(-360.99, 50.44) * mm, "end": v(-360.99, 36.44) * mm});
            skLineSegment(sketch, "E80", {"start": v(-360.99, 36.44) * mm, "end": v(-336.99, 36.44) * mm});
            skLineSegment(sketch, "E81", {"start": v(-336.99, 36.44) * mm, "end": v(-336.99, 50.44) * mm});
            skLineSegment(sketch, "E82", {"start": v(-336.99, 50.44) * mm, "end": v(-317.49, 50.44) * mm});
            skLineSegment(sketch, "E83", {"start": v(-317.49, 50.44) * mm, "end": v(-317.49, 24.44) * mm});
            skLineSegment(sketch, "E84", {"start": v(-317.49, 24.44) * mm, "end": v(-293.49, 24.44) * mm});
            skLineSegment(sketch, "E85", {"start": v(-293.49, 24.44) * mm, "end": v(-293.49, 75.44) * mm});
            skLineSegment(sketch, "E86", {"start": v(-293.49, 75.44) * mm, "end": v(-404.49, 75.44) * mm});
            skLineSegment(sketch, "E87", {"start": v(-380.49, 50.44) * mm, "end": v(-380.49, 75.44) * mm});
            skLineSegment(sketch, "E88", {"start": v(-375.49, 75.44) * mm, "end": v(-375.49, 50.44) * mm});
            skLineSegment(sketch, "E89", {"start": v(-322.49, 50.44) * mm, "end": v(-322.49, 75.44) * mm});
            skLineSegment(sketch, "E90", {"start": v(-317.49, 75.44) * mm, "end": v(-317.49, 50.44) * mm});
            skLineSegment(sketch, "E91", {"start": v(-360.99, 50.44) * mm, "end": v(-351.49, 50.44) * mm});
            skLineSegment(sketch, "E92", {"start": v(-351.49, 75.44) * mm, "end": v(-351.49, 50.44) * mm});
            skLineSegment(sketch, "E93", {"start": v(-346.49, 50.44) * mm, "end": v(-346.49, 75.44) * mm});
            skLineSegment(sketch, "E94", {"start": v(-336.99, 50.44) * mm, "end": v(-346.49, 50.44) * mm});
            skLineSegment(sketch, "E95", {"start": v(-360.99, 48.44) * mm, "end": v(-336.99, 48.44) * mm});
            skSolve(sketch);
        }
        {
            var Q0;
            Q0=makeQuery(id+"F2.imprint","IMPRINT",FACE,{"disambiguationData":[TD([[makeQuery(id+"F2.imprint","IMPRINT",EDGE,{"derivedFrom":sQuery(id+"F2.wireOp",EDGE,"E41.bottom")}),-1.0]])]});
            var Q1;
            {var subQ3=sQuery(id+"F2.wireOp",EDGE,"1b6c74bc-5b00-42bc-9f1d-b8e6521042cd.bottom");Q1=makeQuery(id+"F2.imprint","IMPRINT",FACE,{"disambiguationData":[TD([[makeQuery(id+"F2.imprint","IMPRINT",EDGE,{"derivedFrom":subQ3}),1.0]])]});}
            var Q2;
            {var subQ0=sQuery(id+"F2.wireOp",EDGE,"E87");Q2=makeQuery(id+"F2.imprint","IMPRINT",FACE,{"disambiguationData":[TD([[makeQuery(id+"F2.imprint","IMPRINT",EDGE,{"derivedFrom":subQ0}),-1.0]])]});}
            var Q3;
            {var subQ0=sQuery(id+"F2.wireOp",EDGE,"E91");Q3=makeQuery(id+"F2.imprint","IMPRINT",FACE,{"disambiguationData":[TD([[makeQuery(id+"F2.imprint","IMPRINT",EDGE,{"derivedFrom":subQ0}),-1.0]])]});}
            var Q4;
            {var subQ2=sQuery(id+"F2.wireOp",EDGE,"E89");Q4=makeQuery(id+"F2.imprint","IMPRINT",FACE,{"disambiguationData":[TD([[makeQuery(id+"F2.imprint","IMPRINT",EDGE,{"derivedFrom":subQ2}),-1.0]])]});}
            extrude(context, id + "F3", {"entities" : qUnion([Q0, Q1, Q2, Q3, Q4]), "depth" : 2 * mm});
        }
        {
            var Q0;
            Q0=makeQuery(id+"F1.opExtrude","SWEPT_FACE",FACE,{"disambiguationData":[OSD([sQuery(id+"F0.wireOp",EDGE,"E0.bottom")])]});
            var sketch = newSketch(context, id + "F4", { "sketchPlane" : qUnion([Q0])});
            skLineSegment(sketch, "E96.bottom", {"start": v(-75, 0) * mm, "end": v(-67, 0) * mm});
            skLineSegment(sketch, "E96.top", {"start": v(-75, 7) * mm, "end": v(-67, 7) * mm});
            skLineSegment(sketch, "E96.left", {"start": v(-75, 0) * mm, "end": v(-75, 7) * mm});
            skLineSegment(sketch, "E96.right", {"start": v(-67, 0) * mm, "end": v(-67, 7) * mm});
            skLineSegment(sketch, "E97.bottom", {"start": v(75, 0) * mm, "end": v(67, 0) * mm});
            skLineSegment(sketch, "E97.top", {"start": v(75, 7) * mm, "end": v(67, 7) * mm});
            skLineSegment(sketch, "E97.left", {"start": v(75, 0) * mm, "end": v(75, 7) * mm});
            skLineSegment(sketch, "E97.right", {"start": v(67, 0) * mm, "end": v(67, 7) * mm});
            skSolve(sketch);
        }
        {
            var Q0;
            Q0=qSketchRegion(id+"F4",true);
            extrude(context, id + "F5", {"entities" : qUnion([Q0]), "operationType" : NewBodyOperationType.REMOVE, "oppositeDirection" : true, "depth" : 137.4 * mm});
        }
        {
            var Q0;
            Q0=makeQuery(id+"F1.opExtrude","CAP_FACE",FACE,{"disambiguationData":[OSD([sQuery(id+"F0.wireOp",EDGE,"E0.bottom"),sQuery(id+"F0.wireOp",EDGE,"E0.top"),sQuery(id+"F0.wireOp",EDGE,"E0.left"),sQuery(id+"F0.wireOp",EDGE,"E0.right"),sQuery(id+"F0.wireOp",EDGE,"E3"),sQuery(id+"F0.wireOp",EDGE,"E4"),sQuery(id+"F0.wireOp",EDGE,"E5"),sQuery(id+"F0.wireOp",EDGE,"E6"),sQuery(id+"F0.wireOp",EDGE,"E7"),sQuery(id+"F0.wireOp",EDGE,"E8"),sQuery(id+"F0.wireOp",EDGE,"E9.bottom"),sQuery(id+"F0.wireOp",EDGE,"E9.left"),sQuery(id+"F0.wireOp",EDGE,"E9.right"),sQuery(id+"F0.wireOp",EDGE,"E10.filletArc"),sQuery(id+"F0.wireOp",EDGE,"E11.filletArc"),sQuery(id+"F0.wireOp",EDGE,"E12.bottom"),sQuery(id+"F0.wireOp",EDGE,"E12.left"),sQuery(id+"F0.wireOp",EDGE,"E12.right"),sQuery(id+"F0.wireOp",EDGE,"E13.filletArc"),sQuery(id+"F0.wireOp",EDGE,"E14.filletArc"),sQuery(id+"F0.wireOp",EDGE,"E27"),sQuery(id+"F0.wireOp",EDGE,"E28"),sQuery(id+"F0.wireOp",EDGE,"E29"),sQuery(id+"F0.wireOp",EDGE,"E30"),sQuery(id+"F0.wireOp",EDGE,"E31")])],"isStart":false});
            var sketch = newSketch(context, id + "F6", { "sketchPlane" : qUnion([Q0])});
            skPoint(sketch, "E98.0", {"position": v(-65, 65) * mm});
            skPoint(sketch, "E98.1", {"position": v(65, -65) * mm});
            skLineSegment(sketch, "E99.top", {"start": v(-58.5, -65) * mm, "end": v(58.5, -65) * mm});
            skLineSegment(sketch, "E99.left", {"start": v(-58.5, 2.5) * mm, "end": v(-58.5, -65) * mm});
            skLineSegment(sketch, "E99.right", {"start": v(58.5, 2.5) * mm, "end": v(58.5, -65) * mm});
            skLineSegment(sketch, "E100.bottom", {"start": v(-32.5, -10) * mm, "end": v(32.5, -10) * mm});
            skLineSegment(sketch, "E100.top", {"start": v(-32.5, -65) * mm, "end": v(32.5, -65) * mm});
            skLineSegment(sketch, "E100.left", {"start": v(-32.5, -10) * mm, "end": v(-32.5, -65) * mm});
            skLineSegment(sketch, "E100.right", {"start": v(32.5, -10) * mm, "end": v(32.5, -65) * mm});
            skPoint(sketch, "E101.0", {"position": v(-56.5, 6.5) * mm});
            skPoint(sketch, "E102.3", {"position": v(30.54, 32.33) * mm});
            skPoint(sketch, "E103.0", {"position": v(-26.5, 33.5) * mm});
            skLineSegment(sketch, "E104", {"start": v(-58.5, 2.5) * mm, "end": v(-26.5, 2.5) * mm});
            skPoint(sketch, "E105.0", {"position": v(26.5, 33.5) * mm});
            skLineSegment(sketch, "E106", {"start": v(58.5, 2.5) * mm, "end": v(26.5, 2.5) * mm});
            skLineSegment(sketch, "E107", {"start": v(17, 16) * mm, "end": v(-17, 16) * mm});
            skLineSegment(sketch, "E108", {"start": v(-26.5, 2.5) * mm, "end": v(-26.5, 16) * mm});
            skLineSegment(sketch, "E109", {"start": v(26.5, 2.5) * mm, "end": v(26.5, 16) * mm});
            skLineSegment(sketch, "E110", {"start": v(26.5, 16) * mm, "end": v(17, 16) * mm});
            skLineSegment(sketch, "E111", {"start": v(-17, 16) * mm, "end": v(-26.5, 16) * mm});
            skSolve(sketch);
        }
        {
            var Q0;
            {var subQ6=sQuery(id+"F6.wireOp",EDGE,"E99.left");Q0=makeQuery(id+"F6.imprint","IMPRINT",FACE,{"disambiguationData":[TD([[makeQuery(id+"F6.imprint","IMPRINT",EDGE,{"derivedFrom":subQ6}),1.0]])]});}
            extrude(context, id + "F7", {"entities" : qUnion([Q0]), "operationType" : NewBodyOperationType.REMOVE, "oppositeDirection" : true, "depth" : 3.5 * mm});
        }
        {
            var Q0;
            Q0=makeQuery(id+"F1.opExtrude","CAP_FACE",FACE,{"disambiguationData":[OSD([sQuery(id+"F0.wireOp",EDGE,"E0.bottom"),sQuery(id+"F0.wireOp",EDGE,"E0.top"),sQuery(id+"F0.wireOp",EDGE,"E0.left"),sQuery(id+"F0.wireOp",EDGE,"E0.right"),sQuery(id+"F0.wireOp",EDGE,"E3"),sQuery(id+"F0.wireOp",EDGE,"E4"),sQuery(id+"F0.wireOp",EDGE,"E5"),sQuery(id+"F0.wireOp",EDGE,"E6"),sQuery(id+"F0.wireOp",EDGE,"E7"),sQuery(id+"F0.wireOp",EDGE,"E8"),sQuery(id+"F0.wireOp",EDGE,"E9.bottom"),sQuery(id+"F0.wireOp",EDGE,"E9.left"),sQuery(id+"F0.wireOp",EDGE,"E9.right"),sQuery(id+"F0.wireOp",EDGE,"E10.filletArc"),sQuery(id+"F0.wireOp",EDGE,"E11.filletArc"),sQuery(id+"F0.wireOp",EDGE,"E12.bottom"),sQuery(id+"F0.wireOp",EDGE,"E12.left"),sQuery(id+"F0.wireOp",EDGE,"E12.right"),sQuery(id+"F0.wireOp",EDGE,"E13.filletArc"),sQuery(id+"F0.wireOp",EDGE,"E14.filletArc"),sQuery(id+"F0.wireOp",EDGE,"E27"),sQuery(id+"F0.wireOp",EDGE,"E28"),sQuery(id+"F0.wireOp",EDGE,"E29"),sQuery(id+"F0.wireOp",EDGE,"E30"),sQuery(id+"F0.wireOp",EDGE,"E31")])],"isStart":false});
            var sketch = newSketch(context, id + "F8", { "sketchPlane" : qUnion([Q0])});
            skPoint(sketch, "E112.0", {"position": v(-43.5, 52.5) * mm});
            skPoint(sketch, "E112.1", {"position": v(-43.5, 39.5) * mm});
            skLineSegment(sketch, "E113.bottom", {"start": v(-31.5, 46.5) * mm, "end": v(-55.5, 46.5) * mm});
            skLineSegment(sketch, "E113.top", {"start": v(-31.5, 58.5) * mm, "end": v(-55.5, 58.5) * mm});
            skLineSegment(sketch, "E113.left", {"start": v(-31.5, 46.5) * mm, "end": v(-31.5, 58.5) * mm});
            skLineSegment(sketch, "E113.right", {"start": v(-55.5, 46.5) * mm, "end": v(-55.5, 58.5) * mm});
            skLineSegment(sketch, "E114.bottom", {"start": v(-31.5, 45.5) * mm, "end": v(-55.5, 45.5) * mm});
            skLineSegment(sketch, "E114.top", {"start": v(-31.5, 33.5) * mm, "end": v(-55.5, 33.5) * mm});
            skLineSegment(sketch, "E114.left", {"start": v(-31.5, 45.5) * mm, "end": v(-31.5, 33.5) * mm});
            skLineSegment(sketch, "E114.right", {"start": v(-55.5, 45.5) * mm, "end": v(-55.5, 33.5) * mm});
            skPoint(sketch, "E115.0", {"position": v(-57.5, 57.5) * mm});
            skPoint(sketch, "E115.1", {"position": v(-55.5, 47.5) * mm});
            skPoint(sketch, "E115.2", {"position": v(-31.5, 47.5) * mm});
            skPoint(sketch, "E115.3", {"position": v(-29.5, 57.5) * mm});
            skPoint(sketch, "E115.4", {"position": v(-57.5, 44.5) * mm});
            skPoint(sketch, "E115.5", {"position": v(-55.5, 34.5) * mm});
            skPoint(sketch, "E115.6", {"position": v(-31.5, 34.5) * mm});
            skPoint(sketch, "E115.7", {"position": v(-29.5, 44.5) * mm});
            skLineSegment(sketch, "E116.bottom", {"start": v(-57.5, 57.5) * mm, "end": v(-55.5, 57.5) * mm});
            skLineSegment(sketch, "E116.top", {"start": v(-57.5, 47.5) * mm, "end": v(-55.5, 47.5) * mm});
            skLineSegment(sketch, "E116.left", {"start": v(-57.5, 57.5) * mm, "end": v(-57.5, 47.5) * mm});
            skLineSegment(sketch, "E116.right", {"start": v(-55.5, 57.5) * mm, "end": v(-55.5, 47.5) * mm});
            skLineSegment(sketch, "E117.bottom", {"start": v(-29.5, 57.5) * mm, "end": v(-31.5, 57.5) * mm});
            skLineSegment(sketch, "E117.top", {"start": v(-29.5, 47.5) * mm, "end": v(-31.5, 47.5) * mm});
            skLineSegment(sketch, "E117.left", {"start": v(-29.5, 57.5) * mm, "end": v(-29.5, 47.5) * mm});
            skLineSegment(sketch, "E117.right", {"start": v(-31.5, 57.5) * mm, "end": v(-31.5, 47.5) * mm});
            skLineSegment(sketch, "E118.bottom", {"start": v(-57.5, 44.5) * mm, "end": v(-55.5, 44.5) * mm});
            skLineSegment(sketch, "E118.top", {"start": v(-57.5, 34.5) * mm, "end": v(-55.5, 34.5) * mm});
            skLineSegment(sketch, "E118.left", {"start": v(-57.5, 44.5) * mm, "end": v(-57.5, 34.5) * mm});
            skLineSegment(sketch, "E118.right", {"start": v(-55.5, 44.5) * mm, "end": v(-55.5, 34.5) * mm});
            skLineSegment(sketch, "E119.bottom", {"start": v(-29.5, 44.5) * mm, "end": v(-31.5, 44.5) * mm});
            skLineSegment(sketch, "E119.top", {"start": v(-29.5, 34.5) * mm, "end": v(-31.5, 34.5) * mm});
            skLineSegment(sketch, "E119.left", {"start": v(-29.5, 44.5) * mm, "end": v(-29.5, 34.5) * mm});
            skLineSegment(sketch, "E119.right", {"start": v(-31.5, 44.5) * mm, "end": v(-31.5, 34.5) * mm});
            skPoint(sketch, "E120.0", {"position": v(-43.5, 26.5) * mm});
            skPoint(sketch, "E120.1", {"position": v(-43.5, 13.5) * mm});
            skLineSegment(sketch, "E121.bottom", {"start": v(-31.5, 32.5) * mm, "end": v(-55.5, 32.5) * mm});
            skLineSegment(sketch, "E121.top", {"start": v(-31.5, 20.5) * mm, "end": v(-55.5, 20.5) * mm});
            skLineSegment(sketch, "E121.left", {"start": v(-31.5, 32.5) * mm, "end": v(-31.5, 20.5) * mm});
            skLineSegment(sketch, "E121.right", {"start": v(-55.5, 32.5) * mm, "end": v(-55.5, 20.5) * mm});
            skLineSegment(sketch, "E122.bottom", {"start": v(-31.5, 19.5) * mm, "end": v(-55.5, 19.5) * mm});
            skLineSegment(sketch, "E122.top", {"start": v(-31.5, 7.5) * mm, "end": v(-55.5, 7.5) * mm});
            skLineSegment(sketch, "E122.left", {"start": v(-31.5, 19.5) * mm, "end": v(-31.5, 7.5) * mm});
            skLineSegment(sketch, "E122.right", {"start": v(-55.5, 19.5) * mm, "end": v(-55.5, 7.5) * mm});
            skLineSegment(sketch, "E123.bottom", {"start": v(-55.5, 31.5) * mm, "end": v(-57.5, 31.5) * mm});
            skLineSegment(sketch, "E123.top", {"start": v(-55.5, 21.5) * mm, "end": v(-57.5, 21.5) * mm});
            skLineSegment(sketch, "E123.left", {"start": v(-55.5, 31.5) * mm, "end": v(-55.5, 21.5) * mm});
            skLineSegment(sketch, "E123.right", {"start": v(-57.5, 31.5) * mm, "end": v(-57.5, 21.5) * mm});
            skLineSegment(sketch, "E124.bottom", {"start": v(-55.5, 18.5) * mm, "end": v(-57.5, 18.5) * mm});
            skLineSegment(sketch, "E124.top", {"start": v(-55.5, 8.5) * mm, "end": v(-57.5, 8.5) * mm});
            skLineSegment(sketch, "E124.left", {"start": v(-55.5, 18.5) * mm, "end": v(-55.5, 8.5) * mm});
            skLineSegment(sketch, "E124.right", {"start": v(-57.5, 18.5) * mm, "end": v(-57.5, 8.5) * mm});
            skLineSegment(sketch, "E125.bottom", {"start": v(-31.5, 31.5) * mm, "end": v(-29.5, 31.5) * mm});
            skLineSegment(sketch, "E125.top", {"start": v(-31.5, 21.5) * mm, "end": v(-29.5, 21.5) * mm});
            skLineSegment(sketch, "E125.left", {"start": v(-31.5, 31.5) * mm, "end": v(-31.5, 21.5) * mm});
            skLineSegment(sketch, "E125.right", {"start": v(-29.5, 31.5) * mm, "end": v(-29.5, 21.5) * mm});
            skLineSegment(sketch, "E126.bottom", {"start": v(-31.5, 18.5) * mm, "end": v(-29.5, 18.5) * mm});
            skLineSegment(sketch, "E126.top", {"start": v(-31.5, 8.5) * mm, "end": v(-29.5, 8.5) * mm});
            skLineSegment(sketch, "E126.left", {"start": v(-31.5, 18.5) * mm, "end": v(-31.5, 8.5) * mm});
            skLineSegment(sketch, "E126.right", {"start": v(-29.5, 18.5) * mm, "end": v(-29.5, 8.5) * mm});
            skLineSegment(sketch, "E127.1.0.0", {"start": v(-28.5, 44.5) * mm, "end": v(-28.5, 34.5) * mm});
            skPoint(sketch, "E127.1.0.2", {"position": v(-26.5, 34.5) * mm});
            skPoint(sketch, "E127.1.0.3", {"position": v(-0.5, 44.5) * mm});
            skPoint(sketch, "E127.1.0.5", {"position": v(-14.5, 39.5) * mm});
            skLineSegment(sketch, "E127.1.0.6", {"start": v(-26.5, 57.5) * mm, "end": v(-26.5, 47.5) * mm});
            skPoint(sketch, "E127.1.0.8", {"position": v(-14.5, 52.5) * mm});
            skPoint(sketch, "E127.1.0.10", {"position": v(-0.5, 57.5) * mm});
            skPoint(sketch, "E127.1.0.14", {"position": v(-28.5, 57.5) * mm});
            skLineSegment(sketch, "E127.1.0.15", {"start": v(-0.5, 44.5) * mm, "end": v(-0.5, 34.5) * mm});
            skPoint(sketch, "E127.1.0.17", {"position": v(-28.5, 44.5) * mm});
            skPoint(sketch, "E127.1.0.18", {"position": v(-2.5, 34.5) * mm});
            skLineSegment(sketch, "E127.1.0.20", {"start": v(-0.5, 57.5) * mm, "end": v(-0.5, 47.5) * mm});
            skLineSegment(sketch, "E127.1.0.21", {"start": v(-2.5, 46.5) * mm, "end": v(-26.5, 46.5) * mm});
            skLineSegment(sketch, "E127.1.0.22", {"start": v(-2.5, 58.5) * mm, "end": v(-26.5, 58.5) * mm});
            skLineSegment(sketch, "E127.1.0.23", {"start": v(-28.5, 57.5) * mm, "end": v(-28.5, 47.5) * mm});
            skLineSegment(sketch, "E127.1.0.24", {"start": v(-2.5, 46.5) * mm, "end": v(-2.5, 58.5) * mm});
            skLineSegment(sketch, "E127.1.0.26", {"start": v(-2.5, 45.5) * mm, "end": v(-26.5, 45.5) * mm});
            skPoint(sketch, "E127.1.0.27", {"position": v(-26.5, 47.5) * mm});
            skPoint(sketch, "E127.1.0.28", {"position": v(-2.5, 47.5) * mm});
            skLineSegment(sketch, "E127.1.0.29", {"start": v(-26.5, 45.5) * mm, "end": v(-26.5, 33.5) * mm});
            skLineSegment(sketch, "E127.1.0.30", {"start": v(-2.5, 45.5) * mm, "end": v(-2.5, 33.5) * mm});
            skLineSegment(sketch, "E127.1.0.31", {"start": v(-2.5, 33.5) * mm, "end": v(-26.5, 33.5) * mm});
            skLineSegment(sketch, "E127.1.0.36", {"start": v(-2.5, 44.5) * mm, "end": v(-2.5, 34.5) * mm});
            skPoint(sketch, "E127.1.0.37", {"position": v(-14.5, 52.5) * mm});
            skPoint(sketch, "E127.1.0.39", {"position": v(-14.5, 39.5) * mm});
            skLineSegment(sketch, "E127.1.0.43", {"start": v(-26.5, 44.5) * mm, "end": v(-26.5, 34.5) * mm});
            skLineSegment(sketch, "E127.1.0.44", {"start": v(-2.5, 57.5) * mm, "end": v(-2.5, 47.5) * mm});
            skLineSegment(sketch, "E127.1.0.45", {"start": v(-26.5, 46.5) * mm, "end": v(-26.5, 58.5) * mm});
            skLineSegment(sketch, "E127.1.0.56", {"start": v(-0.5, 57.5) * mm, "end": v(-2.5, 57.5) * mm});
            skLineSegment(sketch, "E127.1.0.57", {"start": v(-0.5, 44.5) * mm, "end": v(-2.5, 44.5) * mm});
            skLineSegment(sketch, "E127.1.0.58", {"start": v(-28.5, 44.5) * mm, "end": v(-26.5, 44.5) * mm});
            skLineSegment(sketch, "E127.1.0.59", {"start": v(-0.5, 47.5) * mm, "end": v(-2.5, 47.5) * mm});
            skLineSegment(sketch, "E127.1.0.60", {"start": v(-28.5, 47.5) * mm, "end": v(-26.5, 47.5) * mm});
            skLineSegment(sketch, "E127.1.0.61", {"start": v(-28.5, 57.5) * mm, "end": v(-26.5, 57.5) * mm});
            skLineSegment(sketch, "E127.1.0.62", {"start": v(-0.5, 34.5) * mm, "end": v(-2.5, 34.5) * mm});
            skLineSegment(sketch, "E127.1.0.63", {"start": v(-28.5, 34.5) * mm, "end": v(-26.5, 34.5) * mm});
            skLineSegment(sketch, "E127.2.0.0", {"start": v(0.5, 44.5) * mm, "end": v(0.5, 34.5) * mm});
            skPoint(sketch, "E127.2.0.2", {"position": v(2.5, 34.5) * mm});
            skPoint(sketch, "E127.2.0.3", {"position": v(28.5, 44.5) * mm});
            skPoint(sketch, "E127.2.0.5", {"position": v(14.5, 39.5) * mm});
            skLineSegment(sketch, "E127.2.0.6", {"start": v(2.5, 57.5) * mm, "end": v(2.5, 47.5) * mm});
            skPoint(sketch, "E127.2.0.8", {"position": v(14.5, 52.5) * mm});
            skPoint(sketch, "E127.2.0.10", {"position": v(28.5, 57.5) * mm});
            skPoint(sketch, "E127.2.0.14", {"position": v(0.5, 57.5) * mm});
            skLineSegment(sketch, "E127.2.0.15", {"start": v(28.5, 44.5) * mm, "end": v(28.5, 34.5) * mm});
            skPoint(sketch, "E127.2.0.17", {"position": v(0.5, 44.5) * mm});
            skPoint(sketch, "E127.2.0.18", {"position": v(26.5, 34.5) * mm});
            skLineSegment(sketch, "E127.2.0.20", {"start": v(28.5, 57.5) * mm, "end": v(28.5, 47.5) * mm});
            skLineSegment(sketch, "E127.2.0.21", {"start": v(26.5, 46.5) * mm, "end": v(2.5, 46.5) * mm});
            skLineSegment(sketch, "E127.2.0.22", {"start": v(26.5, 58.5) * mm, "end": v(2.5, 58.5) * mm});
            skLineSegment(sketch, "E127.2.0.23", {"start": v(0.5, 57.5) * mm, "end": v(0.5, 47.5) * mm});
            skLineSegment(sketch, "E127.2.0.24", {"start": v(26.5, 46.5) * mm, "end": v(26.5, 58.5) * mm});
            skLineSegment(sketch, "E127.2.0.26", {"start": v(26.5, 45.5) * mm, "end": v(2.5, 45.5) * mm});
            skPoint(sketch, "E127.2.0.27", {"position": v(2.5, 47.5) * mm});
            skPoint(sketch, "E127.2.0.28", {"position": v(26.5, 47.5) * mm});
            skLineSegment(sketch, "E127.2.0.29", {"start": v(2.5, 45.5) * mm, "end": v(2.5, 33.5) * mm});
            skLineSegment(sketch, "E127.2.0.30", {"start": v(26.5, 45.5) * mm, "end": v(26.5, 33.5) * mm});
            skLineSegment(sketch, "E127.2.0.31", {"start": v(26.5, 33.5) * mm, "end": v(2.5, 33.5) * mm});
            skLineSegment(sketch, "E127.2.0.36", {"start": v(26.5, 44.5) * mm, "end": v(26.5, 34.5) * mm});
            skPoint(sketch, "E127.2.0.37", {"position": v(14.5, 52.5) * mm});
            skPoint(sketch, "E127.2.0.39", {"position": v(14.5, 39.5) * mm});
            skLineSegment(sketch, "E127.2.0.43", {"start": v(2.5, 44.5) * mm, "end": v(2.5, 34.5) * mm});
            skLineSegment(sketch, "E127.2.0.44", {"start": v(26.5, 57.5) * mm, "end": v(26.5, 47.5) * mm});
            skLineSegment(sketch, "E127.2.0.45", {"start": v(2.5, 46.5) * mm, "end": v(2.5, 58.5) * mm});
            skLineSegment(sketch, "E127.2.0.56", {"start": v(28.5, 57.5) * mm, "end": v(26.5, 57.5) * mm});
            skLineSegment(sketch, "E127.2.0.57", {"start": v(28.5, 44.5) * mm, "end": v(26.5, 44.5) * mm});
            skLineSegment(sketch, "E127.2.0.58", {"start": v(0.5, 44.5) * mm, "end": v(2.5, 44.5) * mm});
            skLineSegment(sketch, "E127.2.0.59", {"start": v(28.5, 47.5) * mm, "end": v(26.5, 47.5) * mm});
            skLineSegment(sketch, "E127.2.0.60", {"start": v(0.5, 47.5) * mm, "end": v(2.5, 47.5) * mm});
            skLineSegment(sketch, "E127.2.0.61", {"start": v(0.5, 57.5) * mm, "end": v(2.5, 57.5) * mm});
            skLineSegment(sketch, "E127.2.0.62", {"start": v(28.5, 34.5) * mm, "end": v(26.5, 34.5) * mm});
            skLineSegment(sketch, "E127.2.0.63", {"start": v(0.5, 34.5) * mm, "end": v(2.5, 34.5) * mm});
            skLineSegment(sketch, "E127.direction1", {"start": v(-57.5, 8.5) * mm, "end": v(-28.5, 8.5) * mm, "construction": true});
            skLineSegment(sketch, "E128.0.3.0", {"start": v(29.5, 44.5) * mm, "end": v(29.5, 34.5) * mm});
            skLineSegment(sketch, "E128.3.3.0", {"start": v(31.5, 19.5) * mm, "end": v(31.5, 7.5) * mm});
            skPoint(sketch, "E128.6.3.0", {"position": v(31.5, 34.5) * mm});
            skPoint(sketch, "E128.7.3.0", {"position": v(57.5, 44.5) * mm});
            skLineSegment(sketch, "E128.8.3.0", {"start": v(55.5, 20.5) * mm, "end": v(31.5, 20.5) * mm});
            skPoint(sketch, "E128.11.3.0", {"position": v(43.5, 39.5) * mm});
            skLineSegment(sketch, "E128.12.3.0", {"start": v(31.5, 57.5) * mm, "end": v(31.5, 47.5) * mm});
            skLineSegment(sketch, "E128.15.3.0", {"start": v(29.5, 18.5) * mm, "end": v(29.5, 8.5) * mm});
            skPoint(sketch, "E128.18.3.0", {"position": v(43.5, 52.5) * mm});
            skLineSegment(sketch, "E128.19.3.0", {"start": v(29.5, 31.5) * mm, "end": v(29.5, 21.5) * mm});
            skPoint(sketch, "E128.22.3.0", {"position": v(57.5, 57.5) * mm});
            skLineSegment(sketch, "E128.23.3.0", {"start": v(55.5, 7.5) * mm, "end": v(31.5, 7.5) * mm});
            skLineSegment(sketch, "E128.26.3.0", {"start": v(55.5, 31.5) * mm, "end": v(55.5, 21.5) * mm});
            skLineSegment(sketch, "E128.29.3.0", {"start": v(57.5, 18.5) * mm, "end": v(57.5, 8.5) * mm});
            skPoint(sketch, "E128.32.3.0", {"position": v(29.5, 57.5) * mm});
            skLineSegment(sketch, "E128.33.3.0", {"start": v(57.5, 44.5) * mm, "end": v(57.5, 34.5) * mm});
            skLineSegment(sketch, "E128.36.3.0", {"start": v(55.5, 32.5) * mm, "end": v(31.5, 32.5) * mm});
            skPoint(sketch, "E128.39.3.0", {"position": v(29.5, 44.5) * mm});
            skPoint(sketch, "E128.40.3.0", {"position": v(55.5, 34.5) * mm});
            skPoint(sketch, "E128.41.3.0", {"position": v(43.5, 13.5) * mm});
            skLineSegment(sketch, "E128.42.3.0", {"start": v(57.5, 57.5) * mm, "end": v(57.5, 47.5) * mm});
            skLineSegment(sketch, "E128.45.3.0", {"start": v(55.5, 46.5) * mm, "end": v(31.5, 46.5) * mm});
            skLineSegment(sketch, "E128.48.3.0", {"start": v(55.5, 58.5) * mm, "end": v(31.5, 58.5) * mm});
            skLineSegment(sketch, "E128.51.3.0", {"start": v(29.5, 57.5) * mm, "end": v(29.5, 47.5) * mm});
            skLineSegment(sketch, "E128.54.3.0", {"start": v(55.5, 46.5) * mm, "end": v(55.5, 58.5) * mm});
            skLineSegment(sketch, "E128.57.3.0", {"start": v(31.5, 32.5) * mm, "end": v(31.5, 20.5) * mm});
            skLineSegment(sketch, "E128.60.3.0", {"start": v(55.5, 45.5) * mm, "end": v(31.5, 45.5) * mm});
            skPoint(sketch, "E128.63.3.0", {"position": v(31.5, 47.5) * mm});
            skPoint(sketch, "E128.64.3.0", {"position": v(55.5, 47.5) * mm});
            skLineSegment(sketch, "E128.65.3.0", {"start": v(31.5, 45.5) * mm, "end": v(31.5, 33.5) * mm});
            skLineSegment(sketch, "E128.68.3.0", {"start": v(55.5, 45.5) * mm, "end": v(55.5, 33.5) * mm});
            skLineSegment(sketch, "E128.71.3.0", {"start": v(55.5, 33.5) * mm, "end": v(31.5, 33.5) * mm});
            skLineSegment(sketch, "E128.74.3.0", {"start": v(57.5, 31.5) * mm, "end": v(57.5, 21.5) * mm});
            skLineSegment(sketch, "E128.77.3.0", {"start": v(55.5, 19.5) * mm, "end": v(31.5, 19.5) * mm});
            skLineSegment(sketch, "E128.80.3.0", {"start": v(55.5, 19.5) * mm, "end": v(55.5, 7.5) * mm});
            skPoint(sketch, "E128.83.3.0", {"position": v(43.5, 26.5) * mm});
            skLineSegment(sketch, "E128.84.3.0", {"start": v(55.5, 44.5) * mm, "end": v(55.5, 34.5) * mm});
            skPoint(sketch, "E128.87.3.0", {"position": v(43.5, 52.5) * mm});
            skLineSegment(sketch, "E128.88.3.0", {"start": v(31.5, 31.5) * mm, "end": v(31.5, 21.5) * mm});
            skPoint(sketch, "E128.91.3.0", {"position": v(43.5, 39.5) * mm});
            skLineSegment(sketch, "E128.92.3.0", {"start": v(55.5, 32.5) * mm, "end": v(55.5, 20.5) * mm});
            skLineSegment(sketch, "E128.95.3.0", {"start": v(31.5, 18.5) * mm, "end": v(31.5, 8.5) * mm});
            skPoint(sketch, "E128.98.3.0", {"position": v(43.5, 13.5) * mm});
            skLineSegment(sketch, "E128.99.3.0", {"start": v(31.5, 44.5) * mm, "end": v(31.5, 34.5) * mm});
            skLineSegment(sketch, "E128.102.3.0", {"start": v(55.5, 57.5) * mm, "end": v(55.5, 47.5) * mm});
            skLineSegment(sketch, "E128.105.3.0", {"start": v(31.5, 46.5) * mm, "end": v(31.5, 58.5) * mm});
            skPoint(sketch, "E128.108.3.0", {"position": v(43.5, 26.5) * mm});
            skLineSegment(sketch, "E128.109.3.0", {"start": v(55.5, 18.5) * mm, "end": v(55.5, 8.5) * mm});
            skLineSegment(sketch, "E128.112.3.0", {"start": v(55.5, 21.5) * mm, "end": v(57.5, 21.5) * mm});
            skLineSegment(sketch, "E128.115.3.0", {"start": v(31.5, 18.5) * mm, "end": v(29.5, 18.5) * mm});
            skLineSegment(sketch, "E128.118.3.0", {"start": v(31.5, 21.5) * mm, "end": v(29.5, 21.5) * mm});
            skLineSegment(sketch, "E128.121.3.0", {"start": v(55.5, 31.5) * mm, "end": v(57.5, 31.5) * mm});
            skLineSegment(sketch, "E128.124.3.0", {"start": v(31.5, 31.5) * mm, "end": v(29.5, 31.5) * mm});
            skLineSegment(sketch, "E128.127.3.0", {"start": v(55.5, 8.5) * mm, "end": v(57.5, 8.5) * mm});
            skLineSegment(sketch, "E128.130.3.0", {"start": v(55.5, 18.5) * mm, "end": v(57.5, 18.5) * mm});
            skLineSegment(sketch, "E128.133.3.0", {"start": v(31.5, 8.5) * mm, "end": v(29.5, 8.5) * mm});
            skLineSegment(sketch, "E128.136.3.0", {"start": v(57.5, 57.5) * mm, "end": v(55.5, 57.5) * mm});
            skLineSegment(sketch, "E128.139.3.0", {"start": v(57.5, 44.5) * mm, "end": v(55.5, 44.5) * mm});
            skLineSegment(sketch, "E128.142.3.0", {"start": v(29.5, 44.5) * mm, "end": v(31.5, 44.5) * mm});
            skLineSegment(sketch, "E128.145.3.0", {"start": v(57.5, 47.5) * mm, "end": v(55.5, 47.5) * mm});
            skLineSegment(sketch, "E128.148.3.0", {"start": v(29.5, 47.5) * mm, "end": v(31.5, 47.5) * mm});
            skLineSegment(sketch, "E128.151.3.0", {"start": v(29.5, 57.5) * mm, "end": v(31.5, 57.5) * mm});
            skLineSegment(sketch, "E128.154.3.0", {"start": v(57.5, 34.5) * mm, "end": v(55.5, 34.5) * mm});
            skLineSegment(sketch, "E128.157.3.0", {"start": v(29.5, 34.5) * mm, "end": v(31.5, 34.5) * mm});
            skPoint(sketch, "E129.0", {"position": v(0, 26.33) * mm});
            skLineSegment(sketch, "E130.bottom", {"start": v(12, 19.5) * mm, "end": v(-12, 19.5) * mm});
            skLineSegment(sketch, "E130.top", {"start": v(12, 31.5) * mm, "end": v(-12, 31.5) * mm});
            skLineSegment(sketch, "E130.left", {"start": v(12, 19.5) * mm, "end": v(12, 31.5) * mm});
            skLineSegment(sketch, "E130.right", {"start": v(-12, 19.5) * mm, "end": v(-12, 31.5) * mm});
            skPoint(sketch, "E130.middle", {"position": v(0, 25.5) * mm});
            skLineSegment(sketch, "E131.bottom", {"start": v(-12, 30.5) * mm, "end": v(-14, 30.5) * mm});
            skLineSegment(sketch, "E131.top", {"start": v(-12, 20.5) * mm, "end": v(-14, 20.5) * mm});
            skLineSegment(sketch, "E131.left", {"start": v(-12, 30.5) * mm, "end": v(-12, 20.5) * mm});
            skLineSegment(sketch, "E131.right", {"start": v(-14, 30.5) * mm, "end": v(-14, 20.5) * mm});
            skLineSegment(sketch, "E132.bottom", {"start": v(12, 30.5) * mm, "end": v(14, 30.5) * mm});
            skLineSegment(sketch, "E132.top", {"start": v(12, 20.5) * mm, "end": v(14, 20.5) * mm});
            skLineSegment(sketch, "E132.left", {"start": v(12, 30.5) * mm, "end": v(12, 20.5) * mm});
            skLineSegment(sketch, "E132.right", {"start": v(14, 30.5) * mm, "end": v(14, 20.5) * mm});
            skSolve(sketch);
        }
        {
            var Q0;
            Q0=qSketchRegion(id+"F8",true);
            extrude(context, id + "F9", {"entities" : qUnion([Q0]), "operationType" : NewBodyOperationType.REMOVE, "oppositeDirection" : true, "depth" : 2 * mm});
        }
        {
            var Q0;
            Q0=makeQuery(id+"F0.imprint","IMPRINT",FACE,{"disambiguationData":[TD([[makeQuery(id+"F0.imprint","IMPRINT",EDGE,{"derivedFrom":sQuery(id+"F0.wireOp",EDGE,"E0.bottom")}),-1.0]])]});
            var sketch = newSketch(context, id + "F10", { "sketchPlane" : qUnion([Q0])});
            skPoint(sketch, "E133.0", {"position": v(65, -65) * mm});
            skPoint(sketch, "E134.0", {"position": v(-44, -17) * mm});
            skLineSegment(sketch, "E135.bottom", {"start": v(58.5, -5) * mm, "end": v(-58.5, -5) * mm});
            skLineSegment(sketch, "E135.top", {"start": v(58.5, -65) * mm, "end": v(-58.5, -65) * mm});
            skLineSegment(sketch, "E135.left", {"start": v(58.5, -5) * mm, "end": v(58.5, -65) * mm});
            skLineSegment(sketch, "E135.right", {"start": v(-58.5, -5) * mm, "end": v(-58.5, -65) * mm});
            skCircle(sketch, "E136.0", {"center": v(0, 3) * mm, "radius": 3.5 * mm});
            skLineSegment(sketch, "E137.bottom", {"start": v(9, 12) * mm, "end": v(-9, 12) * mm});
            skLineSegment(sketch, "E137.top", {"start": v(9, -6) * mm, "end": v(-9, -6) * mm});
            skLineSegment(sketch, "E137.left", {"start": v(9, 12) * mm, "end": v(9, -6) * mm});
            skLineSegment(sketch, "E137.right", {"start": v(-9, 12) * mm, "end": v(-9, -6) * mm});
            skSolve(sketch);
        }
        {
            var Q0;
            Q0=qSketchRegion(id+"F10",true);
            extrude(context, id + "F11", {"entities" : qUnion([Q0]), "operationType" : NewBodyOperationType.REMOVE, "depth" : 5.5 * mm});
        }
        {
            var Q0;
            Q0=makeQuery(id+"F11.boolean.opBoolean","COPY",FACE,{"derivedFrom":makeQuery(id+"F11.opExtrude","CAP_FACE",FACE,{"disambiguationData":[OSD([sQuery(id+"F10.wireOp",EDGE,"E135.bottom"),sQuery(id+"F10.wireOp",EDGE,"E135.top"),sQuery(id+"F10.wireOp",EDGE,"E135.left"),sQuery(id+"F10.wireOp",EDGE,"E135.right")])],"isStart":false})});
            var sketch = newSketch(context, id + "F12", { "sketchPlane" : qUnion([Q0])});
            skLineSegment(sketch, "E138.0", {"start": v(-27.5, 21.5) * mm, "end": v(-14.5, 21.5) * mm});
            skLineSegment(sketch, "E138.1", {"start": v(-14.5, 21.5) * mm, "end": v(-14.5, 40) * mm});
            skLineSegment(sketch, "E138.2", {"start": v(-27.5, 21.5) * mm, "end": v(-27.5, 40) * mm});
            skArc(sketch, "E138.3", {"start": v(-27.5, 40) * mm, "mid": v(-21, 46.5) * mm, "end": v(-14.5, 40) * mm});
            skArc(sketch, "E139", {"start": v(-14.5, 40) * mm, "mid": v(-21, 46.5) * mm, "end": v(-27.5, 40) * mm});
            skCircle(sketch, "E140", {"center": v(-21, 40) * mm, "radius": 5.5 * mm});
            skLineSegment(sketch, "E141.0", {"start": v(-26.5, 22.5) * mm, "end": v(-26.5, 40) * mm});
            skLineSegment(sketch, "E141.1", {"start": v(-26.5, 22.5) * mm, "end": v(-15.5, 22.5) * mm});
            skLineSegment(sketch, "E141.2", {"start": v(-15.5, 22.5) * mm, "end": v(-15.5, 40) * mm});
            skLineSegment(sketch, "E142.1.0.0", {"start": v(14.5, 21.5) * mm, "end": v(27.5, 21.5) * mm});
            skLineSegment(sketch, "E142.1.0.1", {"start": v(14.5, 21.5) * mm, "end": v(14.5, 40) * mm});
            skLineSegment(sketch, "E142.1.0.2", {"start": v(27.5, 21.5) * mm, "end": v(27.5, 40) * mm});
            skArc(sketch, "E142.1.0.3", {"start": v(27.5, 40) * mm, "mid": v(21, 46.5) * mm, "end": v(14.5, 40) * mm});
            skCircle(sketch, "E142.1.0.4", {"center": v(21, 40) * mm, "radius": 5.5 * mm});
            skLineSegment(sketch, "E142.1.0.5", {"start": v(15.5, 22.5) * mm, "end": v(15.5, 40) * mm});
            skLineSegment(sketch, "E142.1.0.6", {"start": v(15.5, 22.5) * mm, "end": v(26.5, 22.5) * mm});
            skLineSegment(sketch, "E142.1.0.7", {"start": v(26.5, 22.5) * mm, "end": v(26.5, 40) * mm});
            skLineSegment(sketch, "E142.1.0.8", {"start": v(14.5, 21.5) * mm, "end": v(14.5, 40) * mm});
            skArc(sketch, "E142.1.0.9", {"start": v(14.5, 40) * mm, "mid": v(21, 46.5) * mm, "end": v(27.5, 40) * mm});
            skLineSegment(sketch, "E142.1.0.10", {"start": v(27.5, 21.5) * mm, "end": v(27.5, 40) * mm});
            skLineSegment(sketch, "E142.1.0.11", {"start": v(14.5, 21.5) * mm, "end": v(27.5, 21.5) * mm});
            skLineSegment(sketch, "E142.direction1", {"start": v(-27.5, 21.5) * mm, "end": v(14.5, 21.5) * mm, "construction": true});
            skCircle(sketch, "E143", {"center": v(0, 49) * mm, "radius": 6 * mm});
            skCircle(sketch, "E144", {"center": v(0, 49) * mm, "radius": 5 * mm});
            skSolve(sketch);
        }
        {
            var Q0;
            Q0=qSketchRegion(id+"F12",true);
            extrude(context, id + "F13", {"entities" : qUnion([Q0]), "operationType" : NewBodyOperationType.ADD, "oppositeDirection" : true, "depth" : 3.5 * mm});
        }
        {
            var Q0;
            Q0=makeQuery(id+"F7.boolean.opBoolean","COPY",FACE,{"derivedFrom":makeQuery(id+"F7.opExtrude","CAP_FACE",FACE,{"disambiguationData":[OSD([sQuery(id+"F0.wireOp",EDGE,"E3"),sQuery(id+"F0.wireOp",EDGE,"E4"),sQuery(id+"F0.wireOp",EDGE,"E5"),sQuery(id+"F0.wireOp",EDGE,"E6"),sQuery(id+"F0.wireOp",EDGE,"E31"),sQuery(id+"F6.wireOp",EDGE,"E99.top"),sQuery(id+"F6.wireOp",EDGE,"E99.left"),sQuery(id+"F6.wireOp",EDGE,"E99.right"),sQuery(id+"F6.wireOp",EDGE,"E100.bottom"),sQuery(id+"F6.wireOp",EDGE,"E100.left"),sQuery(id+"F6.wireOp",EDGE,"E100.right"),sQuery(id+"F6.wireOp",EDGE,"21Ls3SQl-b2cp-nhTs-Hews-Hz9DtT0whMqm"),sQuery(id+"F6.wireOp",EDGE,"h0CnTGEP-4mNU-iRKy-m8ki-n2eBBufmcQq5"),sQuery(id+"F6.wireOp",EDGE,"qAz8Wjot-FG1B-pc5J-QFhs-qNFrgCeN3wRs"),sQuery(id+"F6.wireOp",EDGE,"3BzKvOmG-jRT5-2gjX-6HEZ-JfMvCsTB6kLf"),sQuery(id+"F6.wireOp",EDGE,"7Y8pnDtM-46dH-8U0t-9n2W-nKTeQMZVXlmL"),sQuery(id+"F6.wireOp",EDGE,"64VHZfUW-AVCi-dtqN-Gh6Z-GknAN1bG2Krn"),sQuery(id+"F6.wireOp",EDGE,"LlS92kWC-FErj-klcS-SA7n-WFnKCBPUT4uf"),sQuery(id+"F6.wireOp",EDGE,"mzuXxwp6-lihL-K5XO-aSKc-62nNCRZgz7h9"),sQuery(id+"F6.wireOp",EDGE,"WjnmBHCa-nJvr-w590-o91h-GlZ44agCWnqu"),sQuery(id+"F6.wireOp",EDGE,"ubTacVJG-JOSL-nPcE-mceO-RuthxvDxnQcS")])],"isStart":false})});
            var sketch = newSketch(context, id + "F14", { "sketchPlane" : qUnion([Q0])});
            skPoint(sketch, "E145.0", {"position": v(-62, -65) * mm});
            skPoint(sketch, "E145.1", {"position": v(32.5, -65) * mm});
            skPoint(sketch, "E145.2", {"position": v(-32.5, -65) * mm});
            skPoint(sketch, "E145.3", {"position": v(62, -65) * mm});
            skLineSegment(sketch, "E146.bottom", {"start": v(-62, -30.5) * mm, "end": v(-32.5, -30.5) * mm});
            skLineSegment(sketch, "E146.top", {"start": v(-62, -35.5) * mm, "end": v(-32.5, -35.5) * mm});
            skLineSegment(sketch, "E146.left", {"start": v(-62, -30.5) * mm, "end": v(-62, -35.5) * mm});
            skLineSegment(sketch, "E146.right", {"start": v(-32.5, -30.5) * mm, "end": v(-32.5, -35.5) * mm});
            skLineSegment(sketch, "E147.bottom", {"start": v(32.5, -30.5) * mm, "end": v(62, -30.5) * mm});
            skLineSegment(sketch, "E147.top", {"start": v(32.5, -35.5) * mm, "end": v(62, -35.5) * mm});
            skLineSegment(sketch, "E147.left", {"start": v(32.5, -30.5) * mm, "end": v(32.5, -35.5) * mm});
            skLineSegment(sketch, "E147.right", {"start": v(62, -30.5) * mm, "end": v(62, -35.5) * mm});
            skSolve(sketch);
        }
        {
            var Q0;
            Q0=qSketchRegion(id+"F14",true);
            extrude(context, id + "F15", {"entities" : qUnion([Q0]), "operationType" : NewBodyOperationType.ADD, "depth" : 3.5 * mm});
        }
        {
            var Q0;
            {var subQ3=sQuery(id+"F8.wireOp",EDGE,"E113.bottom");Q0=makeQuery(id+"F8.imprint","IMPRINT",FACE,{"disambiguationData":[TD([[makeQuery(id+"F8.imprint","IMPRINT",EDGE,{"derivedFrom":subQ3}),-1.0]])]});}
            var sketch = newSketch(context, id + "F16", { "sketchPlane" : qUnion([Q0])});
            skPoint(sketch, "E148.0", {"position": v(-55.5, 52.5) * mm});
            skPoint(sketch, "E148.1", {"position": v(-31.5, 52.5) * mm});
            skLineSegment(sketch, "E149.bottom", {"start": v(-55.5, 56.5) * mm, "end": v(-31.5, 56.5) * mm});
            skLineSegment(sketch, "E149.top", {"start": v(-55.5, 54.5) * mm, "end": v(-31.5, 54.5) * mm});
            skLineSegment(sketch, "E149.left", {"start": v(-55.5, 56.5) * mm, "end": v(-55.5, 54.5) * mm});
            skLineSegment(sketch, "E149.right", {"start": v(-31.5, 56.5) * mm, "end": v(-31.5, 54.5) * mm});
            skLineSegment(sketch, "E150.bottom", {"start": v(-55.5, 50.5) * mm, "end": v(-31.5, 50.5) * mm});
            skLineSegment(sketch, "E150.top", {"start": v(-55.5, 48.5) * mm, "end": v(-31.5, 48.5) * mm});
            skLineSegment(sketch, "E150.left", {"start": v(-55.5, 50.5) * mm, "end": v(-55.5, 48.5) * mm});
            skLineSegment(sketch, "E150.right", {"start": v(-31.5, 50.5) * mm, "end": v(-31.5, 48.5) * mm});
            skLineSegment(sketch, "E151.bottom", {"start": v(-55.5, 43.5) * mm, "end": v(-31.5, 43.5) * mm});
            skLineSegment(sketch, "E151.top", {"start": v(-55.5, 41.5) * mm, "end": v(-31.5, 41.5) * mm});
            skLineSegment(sketch, "E151.left", {"start": v(-55.5, 43.5) * mm, "end": v(-55.5, 41.5) * mm});
            skLineSegment(sketch, "E151.right", {"start": v(-31.5, 43.5) * mm, "end": v(-31.5, 41.5) * mm});
            skLineSegment(sketch, "E152.bottom", {"start": v(-55.5, 37.5) * mm, "end": v(-31.5, 37.5) * mm});
            skLineSegment(sketch, "E152.top", {"start": v(-55.5, 35.5) * mm, "end": v(-31.5, 35.5) * mm});
            skLineSegment(sketch, "E152.left", {"start": v(-55.5, 37.5) * mm, "end": v(-55.5, 35.5) * mm});
            skLineSegment(sketch, "E152.right", {"start": v(-31.5, 37.5) * mm, "end": v(-31.5, 35.5) * mm});
            skLineSegment(sketch, "E153.bottom", {"start": v(-55.5, 30.5) * mm, "end": v(-31.5, 30.5) * mm});
            skLineSegment(sketch, "E153.top", {"start": v(-55.5, 28.5) * mm, "end": v(-31.5, 28.5) * mm});
            skLineSegment(sketch, "E153.left", {"start": v(-55.5, 30.5) * mm, "end": v(-55.5, 28.5) * mm});
            skLineSegment(sketch, "E153.right", {"start": v(-31.5, 30.5) * mm, "end": v(-31.5, 28.5) * mm});
            skLineSegment(sketch, "E154.bottom", {"start": v(-55.5, 24.5) * mm, "end": v(-31.5, 24.5) * mm});
            skLineSegment(sketch, "E154.top", {"start": v(-55.5, 22.5) * mm, "end": v(-31.5, 22.5) * mm});
            skLineSegment(sketch, "E154.left", {"start": v(-55.5, 24.5) * mm, "end": v(-55.5, 22.5) * mm});
            skLineSegment(sketch, "E154.right", {"start": v(-31.5, 24.5) * mm, "end": v(-31.5, 22.5) * mm});
            skLineSegment(sketch, "E155.bottom", {"start": v(-55.5, 17.5) * mm, "end": v(-31.5, 17.5) * mm});
            skLineSegment(sketch, "E155.top", {"start": v(-55.5, 15.5) * mm, "end": v(-31.5, 15.5) * mm});
            skLineSegment(sketch, "E155.left", {"start": v(-55.5, 17.5) * mm, "end": v(-55.5, 15.5) * mm});
            skLineSegment(sketch, "E155.right", {"start": v(-31.5, 17.5) * mm, "end": v(-31.5, 15.5) * mm});
            skLineSegment(sketch, "E156.bottom", {"start": v(-55.5, 11.5) * mm, "end": v(-31.5, 11.5) * mm});
            skLineSegment(sketch, "E156.top", {"start": v(-55.5, 9.5) * mm, "end": v(-31.5, 9.5) * mm});
            skLineSegment(sketch, "E156.left", {"start": v(-55.5, 11.5) * mm, "end": v(-55.5, 9.5) * mm});
            skLineSegment(sketch, "E156.right", {"start": v(-31.5, 11.5) * mm, "end": v(-31.5, 9.5) * mm});
            skLineSegment(sketch, "E157.1.0.0", {"start": v(-26.5, 41.5) * mm, "end": v(-2.5, 41.5) * mm});
            skLineSegment(sketch, "E157.1.0.1", {"start": v(-26.5, 43.5) * mm, "end": v(-2.5, 43.5) * mm});
            skLineSegment(sketch, "E157.1.0.2", {"start": v(-26.5, 48.5) * mm, "end": v(-2.5, 48.5) * mm});
            skLineSegment(sketch, "E157.1.0.4", {"start": v(-26.5, 37.5) * mm, "end": v(-2.5, 37.5) * mm});
            skLineSegment(sketch, "E157.1.0.6", {"start": v(-26.5, 50.5) * mm, "end": v(-2.5, 50.5) * mm});
            skLineSegment(sketch, "E157.1.0.7", {"start": v(-26.5, 54.5) * mm, "end": v(-2.5, 54.5) * mm});
            skLineSegment(sketch, "E157.1.0.8", {"start": v(-26.5, 56.5) * mm, "end": v(-2.5, 56.5) * mm});
            skLineSegment(sketch, "E157.1.0.11", {"start": v(-26.5, 35.5) * mm, "end": v(-2.5, 35.5) * mm});
            skPoint(sketch, "E157.1.0.13", {"position": v(-2.5, 52.5) * mm});
            skPoint(sketch, "E157.1.0.16", {"position": v(-26.5, 52.5) * mm});
            skLineSegment(sketch, "E157.1.0.18", {"start": v(-2.5, 50.5) * mm, "end": v(-2.5, 48.5) * mm});
            skLineSegment(sketch, "E157.1.0.19", {"start": v(-26.5, 50.5) * mm, "end": v(-26.5, 48.5) * mm});
            skLineSegment(sketch, "E157.1.0.21", {"start": v(-2.5, 43.5) * mm, "end": v(-2.5, 41.5) * mm});
            skLineSegment(sketch, "E157.1.0.25", {"start": v(-2.5, 56.5) * mm, "end": v(-2.5, 54.5) * mm});
            skLineSegment(sketch, "E157.1.0.26", {"start": v(-26.5, 56.5) * mm, "end": v(-26.5, 54.5) * mm});
            skLineSegment(sketch, "E157.1.0.28", {"start": v(-2.5, 37.5) * mm, "end": v(-2.5, 35.5) * mm});
            skLineSegment(sketch, "E157.1.0.29", {"start": v(-26.5, 37.5) * mm, "end": v(-26.5, 35.5) * mm});
            skLineSegment(sketch, "E157.1.0.30", {"start": v(-26.5, 43.5) * mm, "end": v(-26.5, 41.5) * mm});
            skLineSegment(sketch, "E157.2.0.0", {"start": v(2.5, 41.5) * mm, "end": v(26.5, 41.5) * mm});
            skLineSegment(sketch, "E157.2.0.1", {"start": v(2.5, 43.5) * mm, "end": v(26.5, 43.5) * mm});
            skLineSegment(sketch, "E157.2.0.2", {"start": v(2.5, 48.5) * mm, "end": v(26.5, 48.5) * mm});
            skLineSegment(sketch, "E157.2.0.4", {"start": v(2.5, 37.5) * mm, "end": v(26.5, 37.5) * mm});
            skLineSegment(sketch, "E157.2.0.6", {"start": v(2.5, 50.5) * mm, "end": v(26.5, 50.5) * mm});
            skLineSegment(sketch, "E157.2.0.7", {"start": v(2.5, 54.5) * mm, "end": v(26.5, 54.5) * mm});
            skLineSegment(sketch, "E157.2.0.8", {"start": v(2.5, 56.5) * mm, "end": v(26.5, 56.5) * mm});
            skLineSegment(sketch, "E157.2.0.11", {"start": v(2.5, 35.5) * mm, "end": v(26.5, 35.5) * mm});
            skPoint(sketch, "E157.2.0.13", {"position": v(26.5, 52.5) * mm});
            skPoint(sketch, "E157.2.0.16", {"position": v(2.5, 52.5) * mm});
            skLineSegment(sketch, "E157.2.0.18", {"start": v(26.5, 50.5) * mm, "end": v(26.5, 48.5) * mm});
            skLineSegment(sketch, "E157.2.0.19", {"start": v(2.5, 50.5) * mm, "end": v(2.5, 48.5) * mm});
            skLineSegment(sketch, "E157.2.0.21", {"start": v(26.5, 43.5) * mm, "end": v(26.5, 41.5) * mm});
            skLineSegment(sketch, "E157.2.0.25", {"start": v(26.5, 56.5) * mm, "end": v(26.5, 54.5) * mm});
            skLineSegment(sketch, "E157.2.0.26", {"start": v(2.5, 56.5) * mm, "end": v(2.5, 54.5) * mm});
            skLineSegment(sketch, "E157.2.0.28", {"start": v(26.5, 37.5) * mm, "end": v(26.5, 35.5) * mm});
            skLineSegment(sketch, "E157.2.0.29", {"start": v(2.5, 37.5) * mm, "end": v(2.5, 35.5) * mm});
            skLineSegment(sketch, "E157.2.0.30", {"start": v(2.5, 43.5) * mm, "end": v(2.5, 41.5) * mm});
            skLineSegment(sketch, "E157.3.0.0", {"start": v(31.5, 41.5) * mm, "end": v(55.5, 41.5) * mm});
            skLineSegment(sketch, "E157.3.0.1", {"start": v(31.5, 43.5) * mm, "end": v(55.5, 43.5) * mm});
            skLineSegment(sketch, "E157.3.0.2", {"start": v(31.5, 48.5) * mm, "end": v(55.5, 48.5) * mm});
            skLineSegment(sketch, "E157.3.0.3", {"start": v(31.5, 30.5) * mm, "end": v(55.5, 30.5) * mm});
            skLineSegment(sketch, "E157.3.0.4", {"start": v(31.5, 37.5) * mm, "end": v(55.5, 37.5) * mm});
            skLineSegment(sketch, "E157.3.0.5", {"start": v(31.5, 17.5) * mm, "end": v(55.5, 17.5) * mm});
            skLineSegment(sketch, "E157.3.0.6", {"start": v(31.5, 50.5) * mm, "end": v(55.5, 50.5) * mm});
            skLineSegment(sketch, "E157.3.0.7", {"start": v(31.5, 54.5) * mm, "end": v(55.5, 54.5) * mm});
            skLineSegment(sketch, "E157.3.0.8", {"start": v(31.5, 56.5) * mm, "end": v(55.5, 56.5) * mm});
            skLineSegment(sketch, "E157.3.0.9", {"start": v(31.5, 28.5) * mm, "end": v(55.5, 28.5) * mm});
            skLineSegment(sketch, "E157.3.0.10", {"start": v(31.5, 11.5) * mm, "end": v(55.5, 11.5) * mm});
            skLineSegment(sketch, "E157.3.0.11", {"start": v(31.5, 35.5) * mm, "end": v(55.5, 35.5) * mm});
            skLineSegment(sketch, "E157.3.0.12", {"start": v(31.5, 22.5) * mm, "end": v(55.5, 22.5) * mm});
            skPoint(sketch, "E157.3.0.13", {"position": v(55.5, 52.5) * mm});
            skLineSegment(sketch, "E157.3.0.14", {"start": v(31.5, 9.5) * mm, "end": v(55.5, 9.5) * mm});
            skLineSegment(sketch, "E157.3.0.15", {"start": v(31.5, 24.5) * mm, "end": v(55.5, 24.5) * mm});
            skPoint(sketch, "E157.3.0.16", {"position": v(31.5, 52.5) * mm});
            skLineSegment(sketch, "E157.3.0.17", {"start": v(31.5, 15.5) * mm, "end": v(55.5, 15.5) * mm});
            skLineSegment(sketch, "E157.3.0.18", {"start": v(55.5, 50.5) * mm, "end": v(55.5, 48.5) * mm});
            skLineSegment(sketch, "E157.3.0.19", {"start": v(31.5, 50.5) * mm, "end": v(31.5, 48.5) * mm});
            skLineSegment(sketch, "E157.3.0.20", {"start": v(31.5, 24.5) * mm, "end": v(31.5, 22.5) * mm});
            skLineSegment(sketch, "E157.3.0.21", {"start": v(55.5, 43.5) * mm, "end": v(55.5, 41.5) * mm});
            skLineSegment(sketch, "E157.3.0.22", {"start": v(55.5, 11.5) * mm, "end": v(55.5, 9.5) * mm});
            skLineSegment(sketch, "E157.3.0.23", {"start": v(31.5, 30.5) * mm, "end": v(31.5, 28.5) * mm});
            skLineSegment(sketch, "E157.3.0.24", {"start": v(55.5, 17.5) * mm, "end": v(55.5, 15.5) * mm});
            skLineSegment(sketch, "E157.3.0.25", {"start": v(55.5, 56.5) * mm, "end": v(55.5, 54.5) * mm});
            skLineSegment(sketch, "E157.3.0.26", {"start": v(31.5, 56.5) * mm, "end": v(31.5, 54.5) * mm});
            skLineSegment(sketch, "E157.3.0.27", {"start": v(31.5, 11.5) * mm, "end": v(31.5, 9.5) * mm});
            skLineSegment(sketch, "E157.3.0.28", {"start": v(55.5, 37.5) * mm, "end": v(55.5, 35.5) * mm});
            skLineSegment(sketch, "E157.3.0.29", {"start": v(31.5, 37.5) * mm, "end": v(31.5, 35.5) * mm});
            skLineSegment(sketch, "E157.3.0.30", {"start": v(31.5, 43.5) * mm, "end": v(31.5, 41.5) * mm});
            skLineSegment(sketch, "E157.3.0.31", {"start": v(55.5, 24.5) * mm, "end": v(55.5, 22.5) * mm});
            skLineSegment(sketch, "E157.3.0.32", {"start": v(31.5, 17.5) * mm, "end": v(31.5, 15.5) * mm});
            skLineSegment(sketch, "E157.3.0.33", {"start": v(55.5, 30.5) * mm, "end": v(55.5, 28.5) * mm});
            skLineSegment(sketch, "E157.direction1", {"start": v(-55.5, 9.5) * mm, "end": v(-26.5, 9.5) * mm, "construction": true});
            skPoint(sketch, "E158.0", {"position": v(-12, 19.5) * mm});
            skPoint(sketch, "E158.1", {"position": v(12, 31.5) * mm});
            skLineSegment(sketch, "E159.bottom", {"start": v(-12, 27.5) * mm, "end": v(12, 27.5) * mm});
            skLineSegment(sketch, "E159.top", {"start": v(-12, 29.5) * mm, "end": v(12, 29.5) * mm});
            skLineSegment(sketch, "E159.left", {"start": v(-12, 27.5) * mm, "end": v(-12, 29.5) * mm});
            skLineSegment(sketch, "E159.right", {"start": v(12, 27.5) * mm, "end": v(12, 29.5) * mm});
            skLineSegment(sketch, "E160.bottom", {"start": v(-12, 23.5) * mm, "end": v(12, 23.5) * mm});
            skLineSegment(sketch, "E160.top", {"start": v(-12, 21.5) * mm, "end": v(12, 21.5) * mm});
            skLineSegment(sketch, "E160.left", {"start": v(-12, 23.5) * mm, "end": v(-12, 21.5) * mm});
            skLineSegment(sketch, "E160.right", {"start": v(12, 23.5) * mm, "end": v(12, 21.5) * mm});
            skSolve(sketch);
        }
        {
            var Q0;
            Q0=qCreatedBy(makeId("Top.planeOp"),FACE);
            var sketch = newSketch(context, id + "F17", { "sketchPlane" : qUnion([Q0])});
            skLineSegment(sketch, "E161.bottom", {"start": v(-43.18, 101.93) * mm, "end": v(-67.18, 101.93) * mm});
            skLineSegment(sketch, "E161.top", {"start": v(-43.18, 113.93) * mm, "end": v(-67.18, 113.93) * mm});
            skLineSegment(sketch, "E161.left", {"start": v(-43.18, 101.93) * mm, "end": v(-43.18, 113.93) * mm});
            skLineSegment(sketch, "E161.right", {"start": v(-67.18, 101.93) * mm, "end": v(-67.18, 113.93) * mm});
            skPoint(sketch, "E161.middle", {"position": v(-55.18, 107.93) * mm});
            skLineSegment(sketch, "E162.bottom", {"start": v(-67.18, 112.83) * mm, "end": v(-69.08, 112.83) * mm});
            skLineSegment(sketch, "E162.top", {"start": v(-67.18, 103.03) * mm, "end": v(-69.08, 103.03) * mm});
            skLineSegment(sketch, "E162.left", {"start": v(-67.18, 112.83) * mm, "end": v(-67.18, 103.03) * mm});
            skLineSegment(sketch, "E162.right", {"start": v(-69.08, 112.83) * mm, "end": v(-69.08, 103.03) * mm});
            skLineSegment(sketch, "E163.bottom", {"start": v(-43.18, 112.83) * mm, "end": v(-41.28, 112.83) * mm});
            skLineSegment(sketch, "E163.top", {"start": v(-43.18, 103.03) * mm, "end": v(-41.28, 103.03) * mm});
            skLineSegment(sketch, "E163.left", {"start": v(-43.18, 112.83) * mm, "end": v(-43.18, 103.03) * mm});
            skLineSegment(sketch, "E163.right", {"start": v(-41.28, 112.83) * mm, "end": v(-41.28, 103.03) * mm});
            skSolve(sketch);
        }
        {
            var Q0;
            Q0=qSketchRegion(id+"F17",true);
            extrude(context, id + "F18", {"entities" : qUnion([Q0]), "depth" : 1.9 * mm, "offsetDistance" : 25 * mm});
        }
        {
            var Q0;
            Q0=makeQuery(id+"F18.opExtrude","CAP_FACE",FACE,{"disambiguationData":[OSD([sQuery(id+"F17.wireOp",EDGE,"E161.bottom"),sQuery(id+"F17.wireOp",EDGE,"E161.top"),sQuery(id+"F17.wireOp",EDGE,"E161.left"),sQuery(id+"F17.wireOp",EDGE,"E161.right"),sQuery(id+"F17.wireOp",EDGE,"E162.bottom"),sQuery(id+"F17.wireOp",EDGE,"E162.top"),sQuery(id+"F17.wireOp",EDGE,"E162.right"),sQuery(id+"F17.wireOp",EDGE,"E163.bottom"),sQuery(id+"F17.wireOp",EDGE,"E163.top"),sQuery(id+"F17.wireOp",EDGE,"E163.right")])],"isStart":false});
            var sketch = newSketch(context, id + "F19", { "sketchPlane" : qUnion([Q0])});
            skLineSegment(sketch, "E164.bottom", {"start": v(-67.18, 113.93) * mm, "end": v(-43.18, 113.93) * mm});
            skLineSegment(sketch, "E164.top", {"start": v(-67.18, 101.93) * mm, "end": v(-43.18, 101.93) * mm});
            skLineSegment(sketch, "E164.left", {"start": v(-67.18, 113.93) * mm, "end": v(-67.18, 101.93) * mm});
            skLineSegment(sketch, "E164.right", {"start": v(-43.18, 113.93) * mm, "end": v(-43.18, 101.93) * mm});
            skSolve(sketch);
        }
        {
            var Q0;
            Q0=qSketchRegion(id+"F19",true);
            extrude(context, id + "F20", {"entities" : qUnion([Q0]), "operationType" : NewBodyOperationType.ADD, "depth" : 2 * mm});
        }
        {
            var Q0;
            Q0=makeQuery(id+"F20.opExtrude","CAP_FACE",FACE,{"disambiguationData":[OSD([sQuery(id+"F19.wireOp",EDGE,"E164.bottom"),sQuery(id+"F19.wireOp",EDGE,"E164.top"),sQuery(id+"F19.wireOp",EDGE,"E164.left"),sQuery(id+"F19.wireOp",EDGE,"E164.right")])],"isStart":false});
            var sketch = newSketch(context, id + "F21", { "sketchPlane" : qUnion([Q0])});
            skLineSegment(sketch, "E165.bottom", {"start": v(-44.18, 102.93) * mm, "end": v(-66.18, 102.93) * mm});
            skLineSegment(sketch, "E165.top", {"start": v(-44.18, 112.93) * mm, "end": v(-66.18, 112.93) * mm});
            skLineSegment(sketch, "E165.left", {"start": v(-44.18, 102.93) * mm, "end": v(-44.18, 112.93) * mm});
            skLineSegment(sketch, "E165.right", {"start": v(-66.18, 102.93) * mm, "end": v(-66.18, 112.93) * mm});
            skPoint(sketch, "E165.middle", {"position": v(-55.18, 107.93) * mm});
            skPoint(sketch, "E165.middle.positionSnap0", {"position": v(-55.18, 113.93) * mm});
            skPoint(sketch, "E165.middle.positionSnap1", {"position": v(-67.18, 107.93) * mm});
            skPoint(sketch, "E165.centerSnap0", {"position": v(-55.18, 113.93) * mm});
            skPoint(sketch, "E165.centerSnap1", {"position": v(-67.18, 107.93) * mm});
            skSolve(sketch);
        }
        {
            var Q0;
            Q0=qSketchRegion(id+"F21",true);
            extrude(context, id + "F22", {"entities" : qUnion([Q0]), "operationType" : NewBodyOperationType.ADD, "depth" : 3 * mm, "offsetDistance" : 25 * mm});
        }
        {
            var Q0;
            Q0=makeQuery(id+"F18.opExtrude","CAP_FACE",FACE,{"disambiguationData":[OSD([sQuery(id+"F17.wireOp",EDGE,"E161.bottom"),sQuery(id+"F17.wireOp",EDGE,"E161.top"),sQuery(id+"F17.wireOp",EDGE,"E161.left"),sQuery(id+"F17.wireOp",EDGE,"E161.right"),sQuery(id+"F17.wireOp",EDGE,"E162.bottom"),sQuery(id+"F17.wireOp",EDGE,"E162.top"),sQuery(id+"F17.wireOp",EDGE,"E162.right"),sQuery(id+"F17.wireOp",EDGE,"E163.bottom"),sQuery(id+"F17.wireOp",EDGE,"E163.top"),sQuery(id+"F17.wireOp",EDGE,"E163.right")])],"isStart":true});
            var sketch = newSketch(context, id + "F23", { "sketchPlane" : qUnion([Q0])});
            skLineSegment(sketch, "E166.bottom", {"start": v(-44.18, -112.93) * mm, "end": v(-66.18, -112.93) * mm});
            skLineSegment(sketch, "E166.top", {"start": v(-44.18, -102.93) * mm, "end": v(-66.18, -102.93) * mm});
            skLineSegment(sketch, "E166.left", {"start": v(-44.18, -112.93) * mm, "end": v(-44.18, -102.93) * mm});
            skLineSegment(sketch, "E166.right", {"start": v(-66.18, -112.93) * mm, "end": v(-66.18, -102.93) * mm});
            skPoint(sketch, "E166.middle", {"position": v(-55.18, -107.93) * mm});
            skPoint(sketch, "E166.middle.positionSnap0", {"position": v(-55.18, -101.93) * mm});
            skPoint(sketch, "E166.middle.positionSnap1", {"position": v(-69.08, -107.93) * mm});
            skPoint(sketch, "E166.centerSnap0", {"position": v(-55.18, -101.93) * mm});
            skPoint(sketch, "E166.centerSnap1", {"position": v(-69.08, -107.93) * mm});
            skSolve(sketch);
        }
        {
            var Q0;
            Q0=qSketchRegion(id+"F23",true);
            extrude(context, id + "F24", {"entities" : qUnion([Q0]), "operationType" : NewBodyOperationType.REMOVE, "oppositeDirection" : true, "depth" : 3 * mm});
        }
        {
            var Q0;
            Q0=qSketchRegion(id+"F16",true);
            extrude(context, id + "F25", {"entities" : qUnion([Q0]), "operationType" : NewBodyOperationType.REMOVE, "oppositeDirection" : true, "depth" : 15 * mm});
        }
        {
            var Q0;
            Q0=makeQuery(id+"F0.imprint","IMPRINT",FACE,{"disambiguationData":[TD([[makeQuery(id+"F0.imprint","IMPRINT",EDGE,{"derivedFrom":sQuery(id+"F0.wireOp",EDGE,"E0.bottom")}),-1.0]])]});
            var sketch = newSketch(context, id + "F26", { "sketchPlane" : qUnion([Q0])});
            skLineSegment(sketch, "E167.bottom", {"start": v(60, 61) * mm, "end": v(-60, 61) * mm});
            skLineSegment(sketch, "E167.top", {"start": v(60, 2.5) * mm, "end": v(26.5, 2.5) * mm});
            skLineSegment(sketch, "E167.left", {"start": v(60, 61) * mm, "end": v(60, 2.5) * mm});
            skLineSegment(sketch, "E167.right", {"start": v(-60, 61) * mm, "end": v(-60, 2.5) * mm});
            skLineSegment(sketch, "E168.top", {"start": v(26.5, 16) * mm, "end": v(-26.5, 16) * mm});
            skLineSegment(sketch, "E168.left", {"start": v(26.5, 2.5) * mm, "end": v(26.5, 16) * mm});
            skLineSegment(sketch, "E168.right", {"start": v(-26.5, 2.5) * mm, "end": v(-26.5, 16) * mm});
            skLineSegment(sketch, "E169.trimOffspring", {"start": v(-26.5, 2.5) * mm, "end": v(-60, 2.5) * mm});
            skSolve(sketch);
        }
        {
            var Q0;
            Q0=qSketchRegion(id+"F26",true);
            extrude(context, id + "F27", {"entities" : qUnion([Q0]), "operationType" : NewBodyOperationType.REMOVE, "depth" : 6 * mm});
        }
        {
            var Q0;
            Q0=makeQuery(id+"F13.boolean.opBoolean","MERGE",FACE,{"derivedFrom":[makeQuery(id+"F11.boolean.opBoolean","COPY",FACE,{"derivedFrom":makeQuery(id+"F11.opExtrude","CAP_FACE",FACE,{"disambiguationData":[OSD([sQuery(id+"F10.wireOp",EDGE,"E135.bottom"),sQuery(id+"F10.wireOp",EDGE,"E135.top"),sQuery(id+"F10.wireOp",EDGE,"E135.left"),sQuery(id+"F10.wireOp",EDGE,"E135.right"),sQuery(id+"F10.wireOp",EDGE,"E136.0"),sQuery(id+"F10.wireOp",EDGE,"E137.bottom"),sQuery(id+"F10.wireOp",EDGE,"E137.left"),sQuery(id+"F10.wireOp",EDGE,"E137.right")])],"isStart":false})}),makeQuery(id+"F13.opExtrude","CAP_FACE",FACE,{"disambiguationData":[OSD([sQuery(id+"F12.wireOp",EDGE,"E138.0"),sQuery(id+"F12.wireOp",EDGE,"E138.2"),sQuery(id+"F12.wireOp",EDGE,"E138.1"),sQuery(id+"F12.wireOp",EDGE,"E139"),sQuery(id+"F12.wireOp",EDGE,"E140"),sQuery(id+"F12.wireOp",EDGE,"E141.0"),sQuery(id+"F12.wireOp",EDGE,"E141.1"),sQuery(id+"F12.wireOp",EDGE,"E141.2")])],"isStart":true}),makeQuery(id+"F13.opExtrude","CAP_FACE",FACE,{"disambiguationData":[OSD([sQuery(id+"F12.wireOp",EDGE,"E142.1.0.4"),sQuery(id+"F12.wireOp",EDGE,"E142.1.0.5"),sQuery(id+"F12.wireOp",EDGE,"E142.1.0.6"),sQuery(id+"F12.wireOp",EDGE,"E142.1.0.7"),sQuery(id+"F12.wireOp",EDGE,"E142.1.0.8"),sQuery(id+"F12.wireOp",EDGE,"E142.1.0.9"),sQuery(id+"F12.wireOp",EDGE,"E142.1.0.10"),sQuery(id+"F12.wireOp",EDGE,"E142.1.0.11")])],"isStart":true}),makeQuery(id+"F13.opExtrude","CAP_FACE",FACE,{"disambiguationData":[OSD([sQuery(id+"F12.wireOp",EDGE,"E143"),sQuery(id+"F12.wireOp",EDGE,"E144")])],"isStart":true})]});
            var sketch = newSketch(context, id + "F28", { "sketchPlane" : qUnion([Q0])});
            skLineSegment(sketch, "E170.bottom", {"start": v(1.5, 17.67) * mm, "end": v(-1.5, 17.67) * mm});
            skLineSegment(sketch, "E170.top", {"start": v(1.5, 29.67) * mm, "end": v(-1.5, 29.67) * mm});
            skLineSegment(sketch, "E170.left", {"start": v(1.5, 17.67) * mm, "end": v(1.5, 29.67) * mm});
            skLineSegment(sketch, "E170.right", {"start": v(-1.5, 17.67) * mm, "end": v(-1.5, 29.67) * mm});
            skPoint(sketch, "E170.middle", {"position": v(0, 23.67) * mm});
            skSolve(sketch);
        }
        {
            var Q0;
            {var subQ0=makeQuery(id+"F11.boolean.opBoolean","INTERSECT",EDGE,{"derivedFrom":[makeQuery(id+"F1.opExtrude","SWEPT_FACE",FACE,{"disambiguationData":[OSD([sQuery(id+"F0.wireOp",EDGE,"E8")])]}),makeQuery(id+"F11.opExtrude","CAP_FACE",FACE,{"disambiguationData":[OSD([sQuery(id+"F10.wireOp",EDGE,"E135.bottom"),sQuery(id+"F10.wireOp",EDGE,"E135.top"),sQuery(id+"F10.wireOp",EDGE,"E135.left"),sQuery(id+"F10.wireOp",EDGE,"E135.right"),sQuery(id+"F10.wireOp",EDGE,"E136.0"),sQuery(id+"F10.wireOp",EDGE,"E137.bottom"),sQuery(id+"F10.wireOp",EDGE,"E137.left"),sQuery(id+"F10.wireOp",EDGE,"E137.right")])],"isStart":false})]});var subQ2=sQuery(id+"F28.wireOp",EDGE,"E170.left");var subQ3=makeQuery(id+"F28.imprint","INTERSECT",VERTEX,{"disambiguationData":[OD(0.0)],"derivedFrom":[subQ0,subQ2]});Q0=makeQuery(id+"F28.imprint","IMPRINT",FACE,{"disambiguationData":[TD([[makeQuery(id+"F28.imprint","IMPRINT",EDGE,{"disambiguationData":[TD([[subQ3,-1.0]])],"derivedFrom":subQ2}),1.0]])]});}
            extrude(context, id + "F29", {"entities" : qUnion([Q0]), "operationType" : NewBodyOperationType.ADD, "oppositeDirection" : true, "depth" : 2 * mm, "offsetDistance" : 25 * mm});
        }
        {
            var Q0;
            Q0=makeQuery(id+"F3.opExtrude","CAP_EDGE",EDGE,{"disambiguationData":[OSD([sQuery(id+"F2.wireOp",EDGE,"E41.right")])],"isStart":false});
            var Q1;
            Q1=makeQuery(id+"F3.opExtrude","CAP_EDGE",EDGE,{"disambiguationData":[OSD([sQuery(id+"F2.wireOp",EDGE,"E41.bottom")])],"isStart":false});
            var Q2;
            Q2=makeQuery(id+"F3.opExtrude","CAP_EDGE",EDGE,{"disambiguationData":[OSD([sQuery(id+"F2.wireOp",EDGE,"E41.left")])],"isStart":false});
            var Q3;
            Q3=makeQuery(id+"F3.opExtrude","CAP_EDGE",EDGE,{"disambiguationData":[OSD([sQuery(id+"F2.wireOp",EDGE,"E41.top")])],"isStart":false});
            var Q4;
            Q4=makeQuery(id+"F22.opExtrude","CAP_EDGE",EDGE,{"disambiguationData":[OSD([sQuery(id+"F21.wireOp",EDGE,"E165.right")])],"isStart":false});
            var Q5;
            Q5=makeQuery(id+"F22.opExtrude","CAP_EDGE",EDGE,{"disambiguationData":[OSD([sQuery(id+"F21.wireOp",EDGE,"E165.top")])],"isStart":false});
            var Q6;
            Q6=makeQuery(id+"F22.opExtrude","CAP_EDGE",EDGE,{"disambiguationData":[OSD([sQuery(id+"F21.wireOp",EDGE,"E165.left")])],"isStart":false});
            var Q7;
            Q7=makeQuery(id+"F22.opExtrude","CAP_EDGE",EDGE,{"disambiguationData":[OSD([sQuery(id+"F21.wireOp",EDGE,"E165.bottom")])],"isStart":false});
            fillet(context, id + "F30", {"entities" : qUnion([Q0, Q1, Q2, Q3, Q4, Q5, Q6, Q7]), "radius" : 0.5 * mm, "tangentPropagation" : true, "allowEdgeOverflow" : false});
        }
    });
